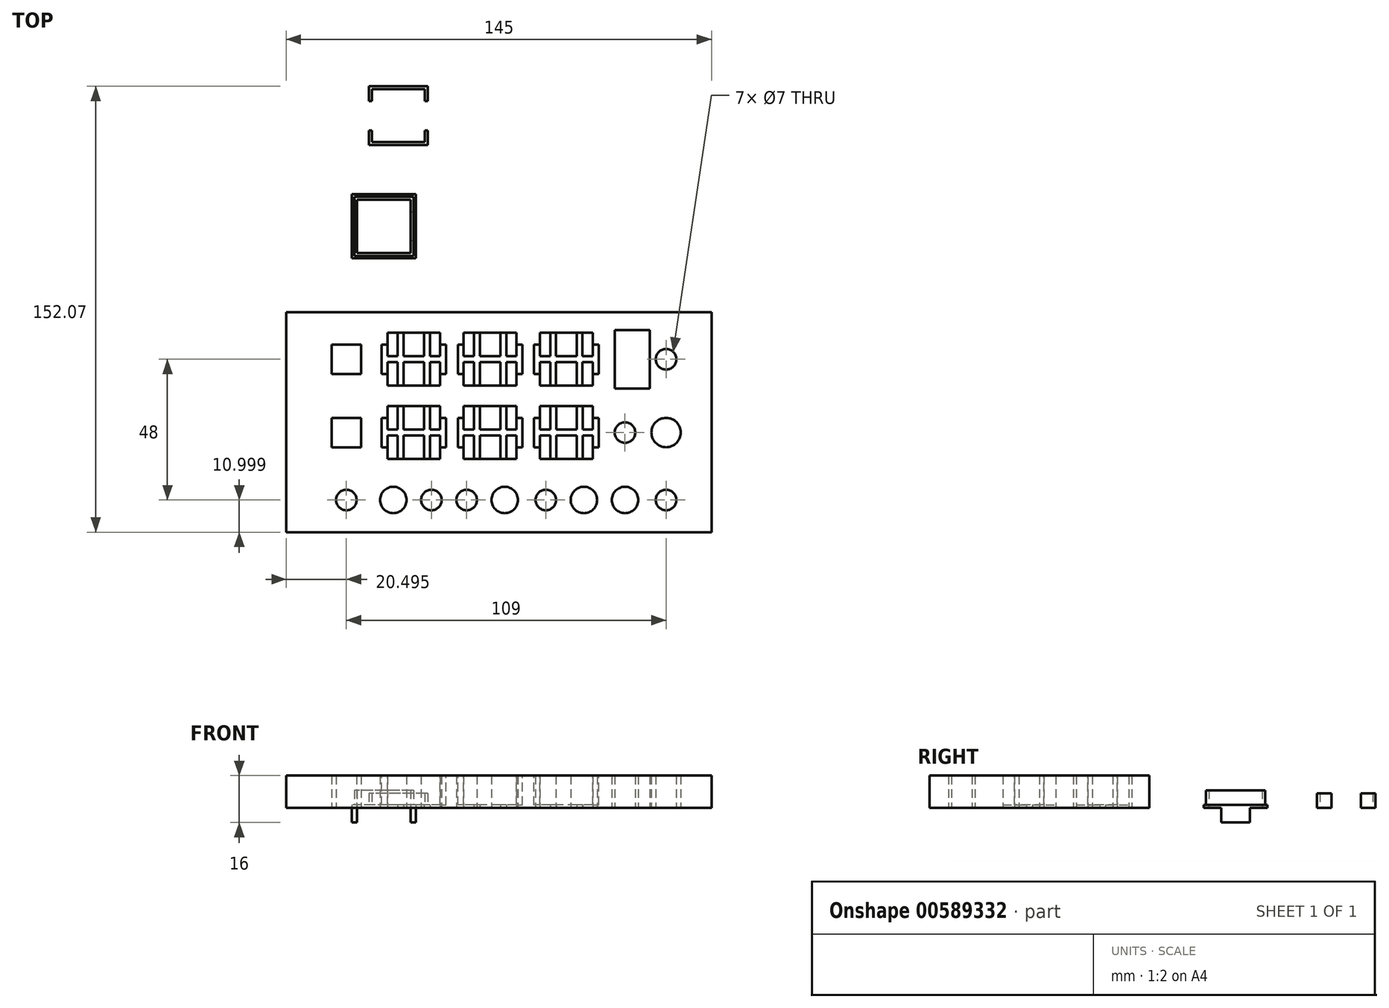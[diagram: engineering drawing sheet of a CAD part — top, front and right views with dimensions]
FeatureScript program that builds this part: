
annotation { "Feature Type Name" : "Feature", "Feature Type Description" : "" }
export const myFeature = defineFeature(function(context is Context, id is Id, definition is map)
    precondition{}
    {
        {
            var Q0;
            Q0=qCreatedBy(makeId("Top.planeOp"),FACE);
            var sketch = newSketch(context, id + "F0", { "sketchPlane" : qUnion([Q0])});
            skLineSegment(sketch, "E0.bottom", {"start": v(-10, -55.04) * mm, "end": v(-155, -55.04) * mm});
            skLineSegment(sketch, "E0.top", {"start": v(-10, 19.96) * mm, "end": v(-155, 19.96) * mm});
            skLineSegment(sketch, "E0.left", {"start": v(-10, -55.04) * mm, "end": v(-10, 19.96) * mm});
            skLineSegment(sketch, "E0.right", {"start": v(-155, -55.04) * mm, "end": v(-155, 19.96) * mm});
            skPoint(sketch, "E0.middle", {"position": v(-82.5, -17.54) * mm});
            skLineSegment(sketch, "E1.bottom", {"start": v(-101.5, -6.04) * mm, "end": v(-121.5, -6.04) * mm, "construction": true});
            skLineSegment(sketch, "E1.top", {"start": v(-101.5, 13.96) * mm, "end": v(-121.5, 13.96) * mm, "construction": true});
            skLineSegment(sketch, "E1.left", {"start": v(-101.5, -6.04) * mm, "end": v(-101.5, 13.96) * mm, "construction": true});
            skLineSegment(sketch, "E1.right", {"start": v(-121.5, -6.04) * mm, "end": v(-121.5, 13.96) * mm, "construction": true});
            skPoint(sketch, "E1.middle", {"position": v(-111.5, 3.96) * mm});
            skLineSegment(sketch, "E2.1.0.0", {"start": v(-95.5, -6.04) * mm, "end": v(-95.5, 13.96) * mm, "construction": true});
            skPoint(sketch, "E2.1.0.1", {"position": v(-85.5, 3.96) * mm});
            skLineSegment(sketch, "E2.1.0.2", {"start": v(-75.5, -6.04) * mm, "end": v(-95.5, -6.04) * mm, "construction": true});
            skLineSegment(sketch, "E2.1.0.3", {"start": v(-75.5, -6.04) * mm, "end": v(-75.5, 13.96) * mm, "construction": true});
            skLineSegment(sketch, "E2.1.0.4", {"start": v(-75.5, 13.96) * mm, "end": v(-95.5, 13.96) * mm, "construction": true});
            skLineSegment(sketch, "E2.2.0.0", {"start": v(-69.5, -6.04) * mm, "end": v(-69.5, 13.96) * mm, "construction": true});
            skPoint(sketch, "E2.2.0.1", {"position": v(-59.5, 3.96) * mm});
            skLineSegment(sketch, "E2.2.0.2", {"start": v(-49.5, -6.04) * mm, "end": v(-69.5, -6.04) * mm, "construction": true});
            skLineSegment(sketch, "E2.2.0.3", {"start": v(-49.5, -6.04) * mm, "end": v(-49.5, 13.96) * mm, "construction": true});
            skLineSegment(sketch, "E2.2.0.4", {"start": v(-49.5, 13.96) * mm, "end": v(-69.5, 13.96) * mm, "construction": true});
            skLineSegment(sketch, "E2.direction1", {"start": v(-121.5, -6.04) * mm, "end": v(-95.5, -6.04) * mm, "construction": true});
            skLineSegment(sketch, "E3.bottom", {"start": v(-101.5, -31.04) * mm, "end": v(-121.5, -31.04) * mm, "construction": true});
            skLineSegment(sketch, "E3.top", {"start": v(-101.5, -11.04) * mm, "end": v(-121.5, -11.04) * mm, "construction": true});
            skLineSegment(sketch, "E3.left", {"start": v(-101.5, -31.04) * mm, "end": v(-101.5, -11.04) * mm, "construction": true});
            skLineSegment(sketch, "E3.right", {"start": v(-121.5, -31.04) * mm, "end": v(-121.5, -11.04) * mm, "construction": true});
            skPoint(sketch, "E3.middle", {"position": v(-111.5, -21.04) * mm});
            skLineSegment(sketch, "E4.1.0.0", {"start": v(-75.5, -31.04) * mm, "end": v(-95.5, -31.04) * mm, "construction": true});
            skLineSegment(sketch, "E4.1.0.1", {"start": v(-75.5, -31.04) * mm, "end": v(-75.5, -11.04) * mm, "construction": true});
            skLineSegment(sketch, "E4.1.0.2", {"start": v(-95.5, -31.04) * mm, "end": v(-95.5, -11.04) * mm, "construction": true});
            skLineSegment(sketch, "E4.1.0.3", {"start": v(-75.5, -11.04) * mm, "end": v(-95.5, -11.04) * mm, "construction": true});
            skPoint(sketch, "E4.1.0.4", {"position": v(-85.5, -21.04) * mm});
            skLineSegment(sketch, "E4.2.0.0", {"start": v(-49.5, -31.04) * mm, "end": v(-69.5, -31.04) * mm, "construction": true});
            skLineSegment(sketch, "E4.2.0.1", {"start": v(-49.5, -31.04) * mm, "end": v(-49.5, -11.04) * mm, "construction": true});
            skLineSegment(sketch, "E4.2.0.2", {"start": v(-69.5, -31.04) * mm, "end": v(-69.5, -11.04) * mm, "construction": true});
            skLineSegment(sketch, "E4.2.0.3", {"start": v(-49.5, -11.04) * mm, "end": v(-69.5, -11.04) * mm, "construction": true});
            skPoint(sketch, "E4.2.0.4", {"position": v(-59.5, -21.04) * mm});
            skLineSegment(sketch, "E4.direction1", {"start": v(-121.5, -31.04) * mm, "end": v(-95.5, -31.04) * mm, "construction": true});
            skCircle(sketch, "E5", {"center": v(-134.5, -44.04) * mm, "radius": 3.5 * mm});
            skCircle(sketch, "E6", {"center": v(-105.5, -44.04) * mm, "radius": 3.5 * mm});
            skCircle(sketch, "E7", {"center": v(-93.5, -44.04) * mm, "radius": 3.5 * mm});
            skLineSegment(sketch, "E8.bottom", {"start": v(-155, 19.96) * mm, "end": v(-147, 19.96) * mm, "construction": true});
            skLineSegment(sketch, "E8.top", {"start": v(-155, -55.04) * mm, "end": v(-147, -55.04) * mm, "construction": true});
            skLineSegment(sketch, "E8.left", {"start": v(-155, 19.96) * mm, "end": v(-155, -55.04) * mm, "construction": true});
            skLineSegment(sketch, "E8.right", {"start": v(-147, 19.96) * mm, "end": v(-147, -55.04) * mm, "construction": true});
            skLineSegment(sketch, "E9.bottom", {"start": v(-10, -55.04) * mm, "end": v(-18, -55.04) * mm, "construction": true});
            skLineSegment(sketch, "E9.top", {"start": v(-10, 19.96) * mm, "end": v(-18, 19.96) * mm, "construction": true});
            skLineSegment(sketch, "E9.left", {"start": v(-10, -55.04) * mm, "end": v(-10, 19.96) * mm, "construction": true});
            skLineSegment(sketch, "E9.right", {"start": v(-18, -55.04) * mm, "end": v(-18, 19.96) * mm, "construction": true});
            skCircle(sketch, "E10", {"center": v(-118.5, -44.04) * mm, "radius": 4.5 * mm});
            skCircle(sketch, "E11", {"center": v(-80.5, -44.04) * mm, "radius": 4.5 * mm});
            skCircle(sketch, "E12", {"center": v(-66.5, -44.04) * mm, "radius": 3.5 * mm});
            skCircle(sketch, "E13", {"center": v(-53.5, -44.04) * mm, "radius": 4.5 * mm});
            skCircle(sketch, "E14", {"center": v(-39.5, -44.04) * mm, "radius": 4.5 * mm});
            skCircle(sketch, "E15", {"center": v(-25.5, -44.04) * mm, "radius": 3.5 * mm});
            skCircle(sketch, "E16", {"center": v(-39.5, -21.04) * mm, "radius": 3.5 * mm});
            skLineSegment(sketch, "E17.bottom", {"start": v(-31, -6.04) * mm, "end": v(-43, -6.04) * mm});
            skLineSegment(sketch, "E17.top", {"start": v(-31, 13.96) * mm, "end": v(-43, 13.96) * mm});
            skLineSegment(sketch, "E17.left", {"start": v(-31, -6.04) * mm, "end": v(-31, 13.96) * mm});
            skLineSegment(sketch, "E17.right", {"start": v(-43, -6.04) * mm, "end": v(-43, 13.96) * mm});
            skPoint(sketch, "E17.middle", {"position": v(-37, 3.96) * mm});
            skCircle(sketch, "E18", {"center": v(-25.5, 3.96) * mm, "radius": 3.5 * mm});
            skCircle(sketch, "E19", {"center": v(-25.5, -21.04) * mm, "radius": 5 * mm});
            skPoint(sketch, "E20.centerSnap0", {"position": v(-121.5, -21.04) * mm});
            skLineSegment(sketch, "E21.bottom", {"start": v(-102.5, -5.04) * mm, "end": v(-120.5, -5.04) * mm});
            skLineSegment(sketch, "E21.top", {"start": v(-102.5, 12.96) * mm, "end": v(-120.5, 12.96) * mm});
            skLineSegment(sketch, "E21.left", {"start": v(-102.5, -5.04) * mm, "end": v(-102.5, 12.96) * mm});
            skLineSegment(sketch, "E21.right", {"start": v(-120.5, -5.04) * mm, "end": v(-120.5, 12.96) * mm});
            skLineSegment(sketch, "E22.bottom", {"start": v(-102.5, -30.04) * mm, "end": v(-120.5, -30.04) * mm});
            skLineSegment(sketch, "E22.top", {"start": v(-102.5, -12.04) * mm, "end": v(-120.5, -12.04) * mm});
            skLineSegment(sketch, "E22.left", {"start": v(-102.5, -30.04) * mm, "end": v(-102.5, -12.04) * mm});
            skLineSegment(sketch, "E22.right", {"start": v(-120.5, -30.04) * mm, "end": v(-120.5, -12.04) * mm});
            skLineSegment(sketch, "E23.bottom", {"start": v(-102.5, 2.96) * mm, "end": v(-106, 2.96) * mm});
            skLineSegment(sketch, "E23.top", {"start": v(-102.5, 4.96) * mm, "end": v(-106, 4.96) * mm});
            skLineSegment(sketch, "E23.left", {"start": v(-102.5, 2.96) * mm, "end": v(-102.5, 4.96) * mm});
            skLineSegment(sketch, "E23.right", {"start": v(-120.5, 2.96) * mm, "end": v(-120.5, 4.96) * mm});
            skLineSegment(sketch, "E24.bottom", {"start": v(-115, -5.04) * mm, "end": v(-117, -5.04) * mm});
            skLineSegment(sketch, "E24.top", {"start": v(-115, 12.96) * mm, "end": v(-117, 12.96) * mm});
            skLineSegment(sketch, "E24.left", {"start": v(-115, -5.04) * mm, "end": v(-115, 2.96) * mm});
            skLineSegment(sketch, "E24.right", {"start": v(-117, -5.04) * mm, "end": v(-117, 2.96) * mm});
            skPoint(sketch, "E24.middle", {"position": v(-116, 3.96) * mm});
            skLineSegment(sketch, "E25.bottom", {"start": v(-106, -5.04) * mm, "end": v(-108, -5.04) * mm});
            skLineSegment(sketch, "E25.top", {"start": v(-106, 12.96) * mm, "end": v(-108, 12.96) * mm});
            skLineSegment(sketch, "E25.left", {"start": v(-106, -5.04) * mm, "end": v(-106, 2.96) * mm});
            skLineSegment(sketch, "E25.right", {"start": v(-108, -5.04) * mm, "end": v(-108, 2.96) * mm});
            skPoint(sketch, "E25.middle", {"position": v(-107, 3.96) * mm});
            skLineSegment(sketch, "E26.trimOffspring", {"start": v(-117, 4.96) * mm, "end": v(-117, 12.96) * mm});
            skLineSegment(sketch, "E27.trimOffspring", {"start": v(-117, 4.96) * mm, "end": v(-120.5, 4.96) * mm});
            skLineSegment(sketch, "E28.trimOffspring", {"start": v(-115, 4.96) * mm, "end": v(-115, 12.96) * mm});
            skLineSegment(sketch, "E29.trimOffspring", {"start": v(-117, 2.96) * mm, "end": v(-120.5, 2.96) * mm});
            skLineSegment(sketch, "E30.trimOffspring", {"start": v(-108, 4.96) * mm, "end": v(-108, 12.96) * mm});
            skLineSegment(sketch, "E31.trimOffspring", {"start": v(-108, 4.96) * mm, "end": v(-115, 4.96) * mm});
            skLineSegment(sketch, "E32.trimOffspring", {"start": v(-106, 4.96) * mm, "end": v(-106, 12.96) * mm});
            skLineSegment(sketch, "E33.trimOffspring", {"start": v(-108, 2.96) * mm, "end": v(-115, 2.96) * mm});
            skLineSegment(sketch, "E34.bottom", {"start": v(-131, -50.54) * mm, "end": v(-138, -50.54) * mm, "construction": true});
            skLineSegment(sketch, "E34.top", {"start": v(-131, -37.54) * mm, "end": v(-138, -37.54) * mm, "construction": true});
            skLineSegment(sketch, "E34.left", {"start": v(-131, -50.54) * mm, "end": v(-131, -37.54) * mm, "construction": true});
            skLineSegment(sketch, "E34.right", {"start": v(-138, -50.54) * mm, "end": v(-138, -37.54) * mm, "construction": true});
            skLineSegment(sketch, "E35.bottom", {"start": v(-102.5, -22.04) * mm, "end": v(-105.98, -22.04) * mm});
            skLineSegment(sketch, "E35.top", {"start": v(-102.5, -20.04) * mm, "end": v(-105.98, -20.04) * mm});
            skLineSegment(sketch, "E35.left", {"start": v(-102.5, -22.04) * mm, "end": v(-102.5, -20.04) * mm});
            skLineSegment(sketch, "E35.right", {"start": v(-120.5, -22.04) * mm, "end": v(-120.5, -20.04) * mm});
            skLineSegment(sketch, "E36.bottom", {"start": v(-114.98, -30.04) * mm, "end": v(-116.98, -30.04) * mm});
            skLineSegment(sketch, "E36.top", {"start": v(-114.98, -12.04) * mm, "end": v(-116.98, -12.04) * mm});
            skLineSegment(sketch, "E36.left", {"start": v(-114.98, -30.04) * mm, "end": v(-114.98, -22.04) * mm});
            skLineSegment(sketch, "E36.right", {"start": v(-116.98, -30.04) * mm, "end": v(-116.98, -22.04) * mm});
            skPoint(sketch, "E36.middle", {"position": v(-115.98, -21.04) * mm});
            skLineSegment(sketch, "E37.bottom", {"start": v(-105.98, -30.04) * mm, "end": v(-107.98, -30.04) * mm});
            skLineSegment(sketch, "E37.top", {"start": v(-105.98, -12.04) * mm, "end": v(-107.98, -12.04) * mm});
            skLineSegment(sketch, "E37.left", {"start": v(-105.98, -30.04) * mm, "end": v(-105.98, -22.04) * mm});
            skLineSegment(sketch, "E37.right", {"start": v(-107.98, -30.04) * mm, "end": v(-107.98, -22.04) * mm});
            skPoint(sketch, "E37.middle", {"position": v(-106.98, -21.04) * mm});
            skLineSegment(sketch, "E38.trimOffspring", {"start": v(-116.98, -20.04) * mm, "end": v(-116.98, -12.04) * mm});
            skLineSegment(sketch, "E39.trimOffspring", {"start": v(-116.98, -20.04) * mm, "end": v(-120.5, -20.04) * mm});
            skLineSegment(sketch, "E40.trimOffspring", {"start": v(-114.98, -20.04) * mm, "end": v(-114.98, -12.04) * mm});
            skLineSegment(sketch, "E41.trimOffspring", {"start": v(-116.98, -22.04) * mm, "end": v(-120.5, -22.04) * mm});
            skLineSegment(sketch, "E42.trimOffspring", {"start": v(-107.98, -20.04) * mm, "end": v(-107.98, -12.04) * mm});
            skLineSegment(sketch, "E43.trimOffspring", {"start": v(-107.98, -20.04) * mm, "end": v(-114.98, -20.04) * mm});
            skLineSegment(sketch, "E44.trimOffspring", {"start": v(-105.98, -20.04) * mm, "end": v(-105.98, -12.04) * mm});
            skLineSegment(sketch, "E45.trimOffspring", {"start": v(-107.98, -22.04) * mm, "end": v(-114.98, -22.04) * mm});
            skLineSegment(sketch, "E46.bottom", {"start": v(-129.5, -1.04) * mm, "end": v(-139.5, -1.04) * mm});
            skLineSegment(sketch, "E46.top", {"start": v(-129.5, 8.96) * mm, "end": v(-139.5, 8.96) * mm});
            skLineSegment(sketch, "E46.left", {"start": v(-129.5, -1.04) * mm, "end": v(-129.5, 8.96) * mm});
            skLineSegment(sketch, "E46.right", {"start": v(-139.5, -1.04) * mm, "end": v(-139.5, 8.96) * mm});
            skPoint(sketch, "E46.middle", {"position": v(-134.5, 3.96) * mm});
            skLineSegment(sketch, "E47.bottom", {"start": v(-129.5, -26.04) * mm, "end": v(-139.5, -26.04) * mm});
            skLineSegment(sketch, "E47.top", {"start": v(-129.5, -16.04) * mm, "end": v(-139.5, -16.04) * mm});
            skLineSegment(sketch, "E47.left", {"start": v(-129.5, -26.04) * mm, "end": v(-129.5, -16.04) * mm});
            skLineSegment(sketch, "E47.right", {"start": v(-139.5, -26.04) * mm, "end": v(-139.5, -16.04) * mm});
            skPoint(sketch, "E47.middle", {"position": v(-134.5, -21.04) * mm});
            skLineSegment(sketch, "E48.1.0.0", {"start": v(-91, 4.96) * mm, "end": v(-91, 12.96) * mm});
            skLineSegment(sketch, "E48.1.0.2", {"start": v(-76.5, -5.04) * mm, "end": v(-76.5, 12.96) * mm});
            skLineSegment(sketch, "E48.1.0.3", {"start": v(-80, -5.04) * mm, "end": v(-80, 2.96) * mm});
            skPoint(sketch, "E48.1.0.4", {"position": v(-90, 3.96) * mm});
            skLineSegment(sketch, "E48.1.0.5", {"start": v(-82, 4.96) * mm, "end": v(-82, 12.96) * mm});
            skLineSegment(sketch, "E48.1.0.6", {"start": v(-80, 4.96) * mm, "end": v(-80, 12.96) * mm});
            skLineSegment(sketch, "E48.1.0.7", {"start": v(-82, 4.96) * mm, "end": v(-89, 4.96) * mm});
            skLineSegment(sketch, "E48.1.0.8", {"start": v(-76.5, 4.96) * mm, "end": v(-80, 4.96) * mm});
            skLineSegment(sketch, "E48.1.0.9", {"start": v(-76.5, 2.96) * mm, "end": v(-80, 2.96) * mm});
            skLineSegment(sketch, "E48.1.0.10", {"start": v(-80, 12.96) * mm, "end": v(-82, 12.96) * mm});
            skPoint(sketch, "E48.1.0.11", {"position": v(-81, 3.96) * mm});
            skLineSegment(sketch, "E48.1.0.12", {"start": v(-91, 4.96) * mm, "end": v(-94.5, 4.96) * mm});
            skLineSegment(sketch, "E48.1.0.13", {"start": v(-91, 2.96) * mm, "end": v(-94.5, 2.96) * mm});
            skLineSegment(sketch, "E48.1.0.14", {"start": v(-89, 4.96) * mm, "end": v(-89, 12.96) * mm});
            skLineSegment(sketch, "E48.1.0.15", {"start": v(-76.5, 12.96) * mm, "end": v(-94.5, 12.96) * mm});
            skLineSegment(sketch, "E48.1.0.16", {"start": v(-91, -5.04) * mm, "end": v(-91, 2.96) * mm});
            skLineSegment(sketch, "E48.1.0.17", {"start": v(-76.5, -5.04) * mm, "end": v(-94.5, -5.04) * mm});
            skLineSegment(sketch, "E48.1.0.18", {"start": v(-89, -5.04) * mm, "end": v(-89, 2.96) * mm});
            skLineSegment(sketch, "E48.1.0.19", {"start": v(-82, -5.04) * mm, "end": v(-82, 2.96) * mm});
            skLineSegment(sketch, "E48.1.0.20", {"start": v(-94.5, -5.04) * mm, "end": v(-94.5, 12.96) * mm});
            skLineSegment(sketch, "E48.1.0.21", {"start": v(-82, 2.96) * mm, "end": v(-89, 2.96) * mm});
            skLineSegment(sketch, "E48.1.0.22", {"start": v(-80, -5.04) * mm, "end": v(-82, -5.04) * mm});
            skLineSegment(sketch, "E48.1.0.23", {"start": v(-76.5, 2.96) * mm, "end": v(-76.5, 4.96) * mm});
            skLineSegment(sketch, "E48.1.0.24", {"start": v(-89, -5.04) * mm, "end": v(-91, -5.04) * mm});
            skLineSegment(sketch, "E48.1.0.25", {"start": v(-94.5, 2.96) * mm, "end": v(-94.5, 4.96) * mm});
            skLineSegment(sketch, "E48.1.0.27", {"start": v(-89, 12.96) * mm, "end": v(-91, 12.96) * mm});
            skLineSegment(sketch, "E48.2.0.0", {"start": v(-65, 4.96) * mm, "end": v(-65, 12.96) * mm});
            skLineSegment(sketch, "E48.2.0.2", {"start": v(-50.5, -5.04) * mm, "end": v(-50.5, 12.96) * mm});
            skLineSegment(sketch, "E48.2.0.3", {"start": v(-54, -5.04) * mm, "end": v(-54, 2.96) * mm});
            skPoint(sketch, "E48.2.0.4", {"position": v(-64, 3.96) * mm});
            skLineSegment(sketch, "E48.2.0.5", {"start": v(-56, 4.96) * mm, "end": v(-56, 12.96) * mm});
            skLineSegment(sketch, "E48.2.0.6", {"start": v(-54, 4.96) * mm, "end": v(-54, 12.96) * mm});
            skLineSegment(sketch, "E48.2.0.7", {"start": v(-56, 4.96) * mm, "end": v(-63, 4.96) * mm});
            skLineSegment(sketch, "E48.2.0.8", {"start": v(-50.5, 4.96) * mm, "end": v(-54, 4.96) * mm});
            skLineSegment(sketch, "E48.2.0.9", {"start": v(-50.5, 2.96) * mm, "end": v(-54, 2.96) * mm});
            skLineSegment(sketch, "E48.2.0.10", {"start": v(-54, 12.96) * mm, "end": v(-56, 12.96) * mm});
            skPoint(sketch, "E48.2.0.11", {"position": v(-55, 3.96) * mm});
            skLineSegment(sketch, "E48.2.0.12", {"start": v(-65, 4.96) * mm, "end": v(-68.5, 4.96) * mm});
            skLineSegment(sketch, "E48.2.0.13", {"start": v(-65, 2.96) * mm, "end": v(-68.5, 2.96) * mm});
            skLineSegment(sketch, "E48.2.0.14", {"start": v(-63, 4.96) * mm, "end": v(-63, 12.96) * mm});
            skLineSegment(sketch, "E48.2.0.15", {"start": v(-50.5, 12.96) * mm, "end": v(-68.5, 12.96) * mm});
            skLineSegment(sketch, "E48.2.0.16", {"start": v(-65, -5.04) * mm, "end": v(-65, 2.96) * mm});
            skLineSegment(sketch, "E48.2.0.17", {"start": v(-50.5, -5.04) * mm, "end": v(-68.5, -5.04) * mm});
            skLineSegment(sketch, "E48.2.0.18", {"start": v(-63, -5.04) * mm, "end": v(-63, 2.96) * mm});
            skLineSegment(sketch, "E48.2.0.19", {"start": v(-56, -5.04) * mm, "end": v(-56, 2.96) * mm});
            skLineSegment(sketch, "E48.2.0.20", {"start": v(-68.5, -5.04) * mm, "end": v(-68.5, 12.96) * mm});
            skLineSegment(sketch, "E48.2.0.21", {"start": v(-56, 2.96) * mm, "end": v(-63, 2.96) * mm});
            skLineSegment(sketch, "E48.2.0.22", {"start": v(-54, -5.04) * mm, "end": v(-56, -5.04) * mm});
            skLineSegment(sketch, "E48.2.0.23", {"start": v(-50.5, 2.96) * mm, "end": v(-50.5, 4.96) * mm});
            skLineSegment(sketch, "E48.2.0.24", {"start": v(-63, -5.04) * mm, "end": v(-65, -5.04) * mm});
            skLineSegment(sketch, "E48.2.0.25", {"start": v(-68.5, 2.96) * mm, "end": v(-68.5, 4.96) * mm});
            skLineSegment(sketch, "E48.2.0.27", {"start": v(-63, 12.96) * mm, "end": v(-65, 12.96) * mm});
            skLineSegment(sketch, "E48.direction1", {"start": v(-120.5, -5.04) * mm, "end": v(-94.5, -5.04) * mm, "construction": true});
            skLineSegment(sketch, "E49.1.0.0", {"start": v(-76.5, -20.04) * mm, "end": v(-79.98, -20.04) * mm});
            skLineSegment(sketch, "E49.1.0.1", {"start": v(-88.98, -20.04) * mm, "end": v(-88.98, -12.04) * mm});
            skLineSegment(sketch, "E49.1.0.2", {"start": v(-81.98, -30.04) * mm, "end": v(-81.98, -22.04) * mm});
            skLineSegment(sketch, "E49.1.0.3", {"start": v(-94.5, -30.04) * mm, "end": v(-94.5, -12.04) * mm});
            skLineSegment(sketch, "E49.1.0.4", {"start": v(-90.98, -30.04) * mm, "end": v(-90.98, -22.04) * mm});
            skLineSegment(sketch, "E49.1.0.5", {"start": v(-76.5, -30.04) * mm, "end": v(-76.5, -12.04) * mm});
            skLineSegment(sketch, "E49.1.0.6", {"start": v(-81.98, -22.04) * mm, "end": v(-88.98, -22.04) * mm});
            skLineSegment(sketch, "E49.1.0.7", {"start": v(-88.98, -30.04) * mm, "end": v(-88.98, -22.04) * mm});
            skLineSegment(sketch, "E49.1.0.9", {"start": v(-79.98, -20.04) * mm, "end": v(-79.98, -12.04) * mm});
            skLineSegment(sketch, "E49.1.0.10", {"start": v(-76.5, -22.04) * mm, "end": v(-79.98, -22.04) * mm});
            skPoint(sketch, "E49.1.0.11", {"position": v(-80.98, -21.04) * mm});
            skLineSegment(sketch, "E49.1.0.12", {"start": v(-90.98, -22.04) * mm, "end": v(-94.5, -22.04) * mm});
            skLineSegment(sketch, "E49.1.0.14", {"start": v(-81.98, -20.04) * mm, "end": v(-88.98, -20.04) * mm});
            skPoint(sketch, "E49.1.0.15", {"position": v(-89.98, -21.04) * mm});
            skLineSegment(sketch, "E49.1.0.16", {"start": v(-79.98, -30.04) * mm, "end": v(-79.98, -22.04) * mm});
            skLineSegment(sketch, "E49.1.0.17", {"start": v(-76.5, -30.04) * mm, "end": v(-94.5, -30.04) * mm});
            skLineSegment(sketch, "E49.1.0.18", {"start": v(-90.98, -20.04) * mm, "end": v(-90.98, -12.04) * mm});
            skLineSegment(sketch, "E49.1.0.19", {"start": v(-81.98, -20.04) * mm, "end": v(-81.98, -12.04) * mm});
            skLineSegment(sketch, "E49.1.0.20", {"start": v(-90.98, -20.04) * mm, "end": v(-94.5, -20.04) * mm});
            skLineSegment(sketch, "E49.1.0.21", {"start": v(-76.5, -12.04) * mm, "end": v(-94.5, -12.04) * mm});
            skLineSegment(sketch, "E49.1.0.22", {"start": v(-88.98, -12.04) * mm, "end": v(-90.98, -12.04) * mm});
            skLineSegment(sketch, "E49.1.0.23", {"start": v(-76.5, -22.04) * mm, "end": v(-76.5, -20.04) * mm});
            skLineSegment(sketch, "E49.1.0.24", {"start": v(-94.5, -22.04) * mm, "end": v(-94.5, -20.04) * mm});
            skLineSegment(sketch, "E49.1.0.26", {"start": v(-94.5, -30.04) * mm, "end": v(-94.5, -12.04) * mm});
            skLineSegment(sketch, "E49.1.0.27", {"start": v(-79.98, -12.04) * mm, "end": v(-81.98, -12.04) * mm});
            skLineSegment(sketch, "E49.1.0.28", {"start": v(-76.5, -30.04) * mm, "end": v(-94.5, -30.04) * mm});
            skLineSegment(sketch, "E49.1.0.29", {"start": v(-76.5, -12.04) * mm, "end": v(-94.5, -12.04) * mm});
            skLineSegment(sketch, "E49.1.0.30", {"start": v(-76.5, -30.04) * mm, "end": v(-76.5, -12.04) * mm});
            skLineSegment(sketch, "E49.1.0.31", {"start": v(-88.98, -30.04) * mm, "end": v(-90.98, -30.04) * mm});
            skLineSegment(sketch, "E49.1.0.32", {"start": v(-79.98, -30.04) * mm, "end": v(-81.98, -30.04) * mm});
            skLineSegment(sketch, "E49.2.0.0", {"start": v(-50.5, -20.04) * mm, "end": v(-53.98, -20.04) * mm});
            skLineSegment(sketch, "E49.2.0.1", {"start": v(-62.98, -20.04) * mm, "end": v(-62.98, -12.04) * mm});
            skLineSegment(sketch, "E49.2.0.2", {"start": v(-55.98, -30.04) * mm, "end": v(-55.98, -22.04) * mm});
            skLineSegment(sketch, "E49.2.0.3", {"start": v(-68.5, -30.04) * mm, "end": v(-68.5, -12.04) * mm});
            skLineSegment(sketch, "E49.2.0.4", {"start": v(-64.98, -30.04) * mm, "end": v(-64.98, -22.04) * mm});
            skLineSegment(sketch, "E49.2.0.5", {"start": v(-50.5, -30.04) * mm, "end": v(-50.5, -12.04) * mm});
            skLineSegment(sketch, "E49.2.0.6", {"start": v(-55.98, -22.04) * mm, "end": v(-62.98, -22.04) * mm});
            skLineSegment(sketch, "E49.2.0.7", {"start": v(-62.98, -30.04) * mm, "end": v(-62.98, -22.04) * mm});
            skLineSegment(sketch, "E49.2.0.9", {"start": v(-53.98, -20.04) * mm, "end": v(-53.98, -12.04) * mm});
            skLineSegment(sketch, "E49.2.0.10", {"start": v(-50.5, -22.04) * mm, "end": v(-53.98, -22.04) * mm});
            skPoint(sketch, "E49.2.0.11", {"position": v(-54.98, -21.04) * mm});
            skLineSegment(sketch, "E49.2.0.12", {"start": v(-64.98, -22.04) * mm, "end": v(-68.5, -22.04) * mm});
            skLineSegment(sketch, "E49.2.0.14", {"start": v(-55.98, -20.04) * mm, "end": v(-62.98, -20.04) * mm});
            skPoint(sketch, "E49.2.0.15", {"position": v(-63.98, -21.04) * mm});
            skLineSegment(sketch, "E49.2.0.16", {"start": v(-53.98, -30.04) * mm, "end": v(-53.98, -22.04) * mm});
            skLineSegment(sketch, "E49.2.0.17", {"start": v(-50.5, -30.04) * mm, "end": v(-68.5, -30.04) * mm});
            skLineSegment(sketch, "E49.2.0.18", {"start": v(-64.98, -20.04) * mm, "end": v(-64.98, -12.04) * mm});
            skLineSegment(sketch, "E49.2.0.19", {"start": v(-55.98, -20.04) * mm, "end": v(-55.98, -12.04) * mm});
            skLineSegment(sketch, "E49.2.0.20", {"start": v(-64.98, -20.04) * mm, "end": v(-68.5, -20.04) * mm});
            skLineSegment(sketch, "E49.2.0.21", {"start": v(-50.5, -12.04) * mm, "end": v(-68.5, -12.04) * mm});
            skLineSegment(sketch, "E49.2.0.22", {"start": v(-62.98, -12.04) * mm, "end": v(-64.98, -12.04) * mm});
            skLineSegment(sketch, "E49.2.0.23", {"start": v(-50.5, -22.04) * mm, "end": v(-50.5, -20.04) * mm});
            skLineSegment(sketch, "E49.2.0.24", {"start": v(-68.5, -22.04) * mm, "end": v(-68.5, -20.04) * mm});
            skLineSegment(sketch, "E49.2.0.26", {"start": v(-68.5, -30.04) * mm, "end": v(-68.5, -12.04) * mm});
            skLineSegment(sketch, "E49.2.0.27", {"start": v(-53.98, -12.04) * mm, "end": v(-55.98, -12.04) * mm});
            skLineSegment(sketch, "E49.2.0.28", {"start": v(-50.5, -30.04) * mm, "end": v(-68.5, -30.04) * mm});
            skLineSegment(sketch, "E49.2.0.29", {"start": v(-50.5, -12.04) * mm, "end": v(-68.5, -12.04) * mm});
            skLineSegment(sketch, "E49.2.0.30", {"start": v(-50.5, -30.04) * mm, "end": v(-50.5, -12.04) * mm});
            skLineSegment(sketch, "E49.2.0.31", {"start": v(-62.98, -30.04) * mm, "end": v(-64.98, -30.04) * mm});
            skLineSegment(sketch, "E49.2.0.32", {"start": v(-53.98, -30.04) * mm, "end": v(-55.98, -30.04) * mm});
            skLineSegment(sketch, "E49.direction1", {"start": v(-120.5, -30.04) * mm, "end": v(-94.5, -30.04) * mm, "construction": true});
            skLineSegment(sketch, "E50.bottom", {"start": v(-133, -1.04) * mm, "end": v(-136, -1.04) * mm});
            skLineSegment(sketch, "E50.top", {"start": v(-133, 8.96) * mm, "end": v(-136, 8.96) * mm});
            skLineSegment(sketch, "E50.left", {"start": v(-133, -1.04) * mm, "end": v(-133, 8.96) * mm});
            skLineSegment(sketch, "E50.right", {"start": v(-136, -1.04) * mm, "end": v(-136, 8.96) * mm});
            skLineSegment(sketch, "E51.bottom", {"start": v(-133, -26.04) * mm, "end": v(-136, -26.04) * mm});
            skLineSegment(sketch, "E51.top", {"start": v(-133, -16.04) * mm, "end": v(-136, -16.04) * mm});
            skLineSegment(sketch, "E51.left", {"start": v(-133, -26.04) * mm, "end": v(-133, -16.04) * mm});
            skLineSegment(sketch, "E51.right", {"start": v(-136, -26.04) * mm, "end": v(-136, -16.04) * mm});
            skSolve(sketch);
        }
        {
            var Q0;
            Q0=makeQuery(id+"F0.imprint","IMPRINT",FACE,{"disambiguationData":[TD([[makeQuery(id+"F0.imprint","IMPRINT",EDGE,{"derivedFrom":sQuery(id+"F0.wireOp",EDGE,"E0.bottom")}),-1.0]])]});
            var Q1;
            Q1=makeQuery(id+"F0.imprint","IMPRINT",FACE,{"disambiguationData":[TD([[makeQuery(id+"F0.imprint","IMPRINT",EDGE,{"derivedFrom":sQuery(id+"F0.wireOp",EDGE,"E23.bottom")}),-1.0]])]});
            var Q2;
            Q2=makeQuery(id+"F0.imprint","IMPRINT",FACE,{"disambiguationData":[TD([[makeQuery(id+"F0.imprint","IMPRINT",EDGE,{"derivedFrom":sQuery(id+"F0.wireOp",EDGE,"E35.bottom")}),-1.0]])]});
            var Q3;
            Q3=makeQuery(id+"F0.imprint","IMPRINT",FACE,{"disambiguationData":[TD([[makeQuery(id+"F0.imprint","IMPRINT",EDGE,{"derivedFrom":sQuery(id+"F0.wireOp",EDGE,"E48.1.0.0")}),-1.0]])]});
            var Q4;
            Q4=makeQuery(id+"F0.imprint","IMPRINT",FACE,{"disambiguationData":[TD([[makeQuery(id+"F0.imprint","IMPRINT",EDGE,{"derivedFrom":sQuery(id+"F0.wireOp",EDGE,"E48.2.0.0")}),-1.0]])]});
            var Q5;
            {var subQ3=sQuery(id+"F0.wireOp",EDGE,"E49.2.0.0");Q5=makeQuery(id+"F0.imprint","IMPRINT",FACE,{"disambiguationData":[TD([[makeQuery(id+"F0.imprint","IMPRINT",EDGE,{"derivedFrom":subQ3}),1.0]])]});}
            var Q6;
            {var subQ3=sQuery(id+"F0.wireOp",EDGE,"E49.1.0.0");Q6=makeQuery(id+"F0.imprint","IMPRINT",FACE,{"disambiguationData":[TD([[makeQuery(id+"F0.imprint","IMPRINT",EDGE,{"derivedFrom":subQ3}),1.0]])]});}
            var Q7;
            Q7=makeQuery(id+"F0.imprint","IMPRINT",FACE,{"disambiguationData":[TD([[makeQuery(id+"F0.imprint","IMPRINT",EDGE,{"derivedFrom":sQuery(id+"F0.wireOp",EDGE,"E50.bottom")}),-1.0]])]});
            var Q8;
            Q8=makeQuery(id+"F0.imprint","IMPRINT",FACE,{"disambiguationData":[TD([[makeQuery(id+"F0.imprint","IMPRINT",EDGE,{"derivedFrom":sQuery(id+"F0.wireOp",EDGE,"E51.bottom")}),-1.0]])]});
            extrude(context, id + "F1", {"entities" : qUnion([Q0, Q1, Q2, Q3, Q4, Q5, Q6, Q7, Q8]), "depth" : 1 * mm});
        }
        {
            var Q0;
            Q0=makeQuery(id+"F1.opExtrude","CAP_FACE",FACE,{"disambiguationData":[OSD([sQuery(id+"F0.wireOp",EDGE,"E0.bottom"),sQuery(id+"F0.wireOp",EDGE,"E0.top"),sQuery(id+"F0.wireOp",EDGE,"E0.left"),sQuery(id+"F0.wireOp",EDGE,"E0.right"),sQuery(id+"F0.wireOp",EDGE,"E5"),sQuery(id+"F0.wireOp",EDGE,"E6"),sQuery(id+"F0.wireOp",EDGE,"E7"),sQuery(id+"F0.wireOp",EDGE,"E10"),sQuery(id+"F0.wireOp",EDGE,"E11"),sQuery(id+"F0.wireOp",EDGE,"E12"),sQuery(id+"F0.wireOp",EDGE,"E13"),sQuery(id+"F0.wireOp",EDGE,"E14"),sQuery(id+"F0.wireOp",EDGE,"E15"),sQuery(id+"F0.wireOp",EDGE,"E16"),sQuery(id+"F0.wireOp",EDGE,"E17.bottom"),sQuery(id+"F0.wireOp",EDGE,"E17.top"),sQuery(id+"F0.wireOp",EDGE,"E17.left"),sQuery(id+"F0.wireOp",EDGE,"E17.right"),sQuery(id+"F0.wireOp",EDGE,"E18"),sQuery(id+"F0.wireOp",EDGE,"E19"),sQuery(id+"F0.wireOp",EDGE,"E21.bottom"),sQuery(id+"F0.wireOp",EDGE,"E21.top"),sQuery(id+"F0.wireOp",EDGE,"E21.left"),sQuery(id+"F0.wireOp",EDGE,"E21.right"),sQuery(id+"F0.wireOp",EDGE,"E23.bottom"),sQuery(id+"F0.wireOp",EDGE,"E23.top"),sQuery(id+"F0.wireOp",EDGE,"E24.left"),sQuery(id+"F0.wireOp",EDGE,"E24.right"),sQuery(id+"F0.wireOp",EDGE,"E25.left"),sQuery(id+"F0.wireOp",EDGE,"E25.right"),sQuery(id+"F0.wireOp",EDGE,"E26.trimOffspring"),sQuery(id+"F0.wireOp",EDGE,"E27.trimOffspring"),sQuery(id+"F0.wireOp",EDGE,"E28.trimOffspring"),sQuery(id+"F0.wireOp",EDGE,"E29.trimOffspring"),sQuery(id+"F0.wireOp",EDGE,"E30.trimOffspring"),sQuery(id+"F0.wireOp",EDGE,"E31.trimOffspring"),sQuery(id+"F0.wireOp",EDGE,"E32.trimOffspring"),sQuery(id+"F0.wireOp",EDGE,"E33.trimOffspring"),sQuery(id+"F0.wireOp",EDGE,"E22.bottom"),sQuery(id+"F0.wireOp",EDGE,"E22.top"),sQuery(id+"F0.wireOp",EDGE,"E22.left"),sQuery(id+"F0.wireOp",EDGE,"E22.right"),sQuery(id+"F0.wireOp",EDGE,"E35.bottom"),sQuery(id+"F0.wireOp",EDGE,"E35.top"),sQuery(id+"F0.wireOp",EDGE,"E36.left"),sQuery(id+"F0.wireOp",EDGE,"E36.right"),sQuery(id+"F0.wireOp",EDGE,"E37.left"),sQuery(id+"F0.wireOp",EDGE,"E37.right"),sQuery(id+"F0.wireOp",EDGE,"E38.trimOffspring"),sQuery(id+"F0.wireOp",EDGE,"E39.trimOffspring"),sQuery(id+"F0.wireOp",EDGE,"E40.trimOffspring"),sQuery(id+"F0.wireOp",EDGE,"E41.trimOffspring"),sQuery(id+"F0.wireOp",EDGE,"E42.trimOffspring"),sQuery(id+"F0.wireOp",EDGE,"E43.trimOffspring"),sQuery(id+"F0.wireOp",EDGE,"E44.trimOffspring"),sQuery(id+"F0.wireOp",EDGE,"E45.trimOffspring"),sQuery(id+"F0.wireOp",EDGE,"E46.bottom"),sQuery(id+"F0.wireOp",EDGE,"E46.top"),sQuery(id+"F0.wireOp",EDGE,"E46.left"),sQuery(id+"F0.wireOp",EDGE,"E46.right"),sQuery(id+"F0.wireOp",EDGE,"E47.bottom"),sQuery(id+"F0.wireOp",EDGE,"E47.top"),sQuery(id+"F0.wireOp",EDGE,"E47.left"),sQuery(id+"F0.wireOp",EDGE,"E47.right"),sQuery(id+"F0.wireOp",EDGE,"E48.1.0.0"),sQuery(id+"F0.wireOp",EDGE,"E48.1.0.2"),sQuery(id+"F0.wireOp",EDGE,"E48.1.0.3"),sQuery(id+"F0.wireOp",EDGE,"E48.1.0.5"),sQuery(id+"F0.wireOp",EDGE,"E48.1.0.6"),sQuery(id+"F0.wireOp",EDGE,"E48.1.0.7"),sQuery(id+"F0.wireOp",EDGE,"E48.1.0.8"),sQuery(id+"F0.wireOp",EDGE,"E48.1.0.9"),sQuery(id+"F0.wireOp",EDGE,"E48.1.0.12"),sQuery(id+"F0.wireOp",EDGE,"E48.1.0.13"),sQuery(id+"F0.wireOp",EDGE,"E48.1.0.14"),sQuery(id+"F0.wireOp",EDGE,"E48.1.0.15"),sQuery(id+"F0.wireOp",EDGE,"E48.1.0.16"),sQuery(id+"F0.wireOp",EDGE,"E48.1.0.17"),sQuery(id+"F0.wireOp",EDGE,"E48.1.0.18"),sQuery(id+"F0.wireOp",EDGE,"E48.1.0.19"),sQuery(id+"F0.wireOp",EDGE,"E48.1.0.20"),sQuery(id+"F0.wireOp",EDGE,"E48.1.0.21"),sQuery(id+"F0.wireOp",EDGE,"E48.2.0.0"),sQuery(id+"F0.wireOp",EDGE,"E48.2.0.2"),sQuery(id+"F0.wireOp",EDGE,"E48.2.0.3"),sQuery(id+"F0.wireOp",EDGE,"E48.2.0.5"),sQuery(id+"F0.wireOp",EDGE,"E48.2.0.6"),sQuery(id+"F0.wireOp",EDGE,"E48.2.0.7"),sQuery(id+"F0.wireOp",EDGE,"E48.2.0.8"),sQuery(id+"F0.wireOp",EDGE,"E48.2.0.9"),sQuery(id+"F0.wireOp",EDGE,"E48.2.0.12"),sQuery(id+"F0.wireOp",EDGE,"E48.2.0.13"),sQuery(id+"F0.wireOp",EDGE,"E48.2.0.14"),sQuery(id+"F0.wireOp",EDGE,"E48.2.0.15"),sQuery(id+"F0.wireOp",EDGE,"E48.2.0.16"),sQuery(id+"F0.wireOp",EDGE,"E48.2.0.17"),sQuery(id+"F0.wireOp",EDGE,"E48.2.0.18"),sQuery(id+"F0.wireOp",EDGE,"E48.2.0.19"),sQuery(id+"F0.wireOp",EDGE,"E48.2.0.20"),sQuery(id+"F0.wireOp",EDGE,"E48.2.0.21"),sQuery(id+"F0.wireOp",EDGE,"E49.1.0.0"),sQuery(id+"F0.wireOp",EDGE,"E49.1.0.1"),sQuery(id+"F0.wireOp",EDGE,"E49.1.0.2"),sQuery(id+"F0.wireOp",EDGE,"E49.1.0.4"),sQuery(id+"F0.wireOp",EDGE,"E49.1.0.6"),sQuery(id+"F0.wireOp",EDGE,"E49.1.0.7"),sQuery(id+"F0.wireOp",EDGE,"E49.1.0.9"),sQuery(id+"F0.wireOp",EDGE,"E49.1.0.10"),sQuery(id+"F0.wireOp",EDGE,"E49.1.0.12"),sQuery(id+"F0.wireOp",EDGE,"E49.1.0.14"),sQuery(id+"F0.wireOp",EDGE,"E49.1.0.16"),sQuery(id+"F0.wireOp",EDGE,"E49.1.0.18"),sQuery(id+"F0.wireOp",EDGE,"E49.1.0.19"),sQuery(id+"F0.wireOp",EDGE,"E49.1.0.20"),sQuery(id+"F0.wireOp",EDGE,"E49.1.0.26"),sQuery(id+"F0.wireOp",EDGE,"E49.1.0.28"),sQuery(id+"F0.wireOp",EDGE,"E49.1.0.29"),sQuery(id+"F0.wireOp",EDGE,"E49.1.0.30"),sQuery(id+"F0.wireOp",EDGE,"E49.2.0.0"),sQuery(id+"F0.wireOp",EDGE,"E49.2.0.1"),sQuery(id+"F0.wireOp",EDGE,"E49.2.0.2"),sQuery(id+"F0.wireOp",EDGE,"E49.2.0.4"),sQuery(id+"F0.wireOp",EDGE,"E49.2.0.6"),sQuery(id+"F0.wireOp",EDGE,"E49.2.0.7"),sQuery(id+"F0.wireOp",EDGE,"E49.2.0.9"),sQuery(id+"F0.wireOp",EDGE,"E49.2.0.10"),sQuery(id+"F0.wireOp",EDGE,"E49.2.0.12"),sQuery(id+"F0.wireOp",EDGE,"E49.2.0.14"),sQuery(id+"F0.wireOp",EDGE,"E49.2.0.16"),sQuery(id+"F0.wireOp",EDGE,"E49.2.0.18"),sQuery(id+"F0.wireOp",EDGE,"E49.2.0.19"),sQuery(id+"F0.wireOp",EDGE,"E49.2.0.20"),sQuery(id+"F0.wireOp",EDGE,"E49.2.0.26"),sQuery(id+"F0.wireOp",EDGE,"E49.2.0.28"),sQuery(id+"F0.wireOp",EDGE,"E49.2.0.29"),sQuery(id+"F0.wireOp",EDGE,"E49.2.0.30")])],"isStart":false});
            extrude(context, id + "F2", {"entities" : qUnion([Q0]), "operationType" : NewBodyOperationType.ADD, "depth" : 10 * mm});
        }
        {
            var Q0;
            Q0=makeQuery(id+"F2.opExtrude","CAP_FACE",FACE,{"disambiguationData":[OSD([sQuery(id+"F0.wireOp",EDGE,"E0.bottom"),sQuery(id+"F0.wireOp",EDGE,"E0.top"),sQuery(id+"F0.wireOp",EDGE,"E0.left"),sQuery(id+"F0.wireOp",EDGE,"E0.right"),sQuery(id+"F0.wireOp",EDGE,"E5"),sQuery(id+"F0.wireOp",EDGE,"E6"),sQuery(id+"F0.wireOp",EDGE,"E7"),sQuery(id+"F0.wireOp",EDGE,"E10"),sQuery(id+"F0.wireOp",EDGE,"E11"),sQuery(id+"F0.wireOp",EDGE,"E12"),sQuery(id+"F0.wireOp",EDGE,"E13"),sQuery(id+"F0.wireOp",EDGE,"E14"),sQuery(id+"F0.wireOp",EDGE,"E15"),sQuery(id+"F0.wireOp",EDGE,"E16"),sQuery(id+"F0.wireOp",EDGE,"E17.bottom"),sQuery(id+"F0.wireOp",EDGE,"E17.top"),sQuery(id+"F0.wireOp",EDGE,"E17.left"),sQuery(id+"F0.wireOp",EDGE,"E17.right"),sQuery(id+"F0.wireOp",EDGE,"E18"),sQuery(id+"F0.wireOp",EDGE,"E19"),sQuery(id+"F0.wireOp",EDGE,"E21.bottom"),sQuery(id+"F0.wireOp",EDGE,"E21.top"),sQuery(id+"F0.wireOp",EDGE,"E21.left"),sQuery(id+"F0.wireOp",EDGE,"E21.right"),sQuery(id+"F0.wireOp",EDGE,"E23.bottom"),sQuery(id+"F0.wireOp",EDGE,"E23.top"),sQuery(id+"F0.wireOp",EDGE,"E24.left"),sQuery(id+"F0.wireOp",EDGE,"E24.right"),sQuery(id+"F0.wireOp",EDGE,"E25.left"),sQuery(id+"F0.wireOp",EDGE,"E25.right"),sQuery(id+"F0.wireOp",EDGE,"E26.trimOffspring"),sQuery(id+"F0.wireOp",EDGE,"E27.trimOffspring"),sQuery(id+"F0.wireOp",EDGE,"E28.trimOffspring"),sQuery(id+"F0.wireOp",EDGE,"E29.trimOffspring"),sQuery(id+"F0.wireOp",EDGE,"E30.trimOffspring"),sQuery(id+"F0.wireOp",EDGE,"E31.trimOffspring"),sQuery(id+"F0.wireOp",EDGE,"E32.trimOffspring"),sQuery(id+"F0.wireOp",EDGE,"E33.trimOffspring"),sQuery(id+"F0.wireOp",EDGE,"E22.bottom"),sQuery(id+"F0.wireOp",EDGE,"E22.top"),sQuery(id+"F0.wireOp",EDGE,"E22.left"),sQuery(id+"F0.wireOp",EDGE,"E22.right"),sQuery(id+"F0.wireOp",EDGE,"E35.bottom"),sQuery(id+"F0.wireOp",EDGE,"E35.top"),sQuery(id+"F0.wireOp",EDGE,"E36.left"),sQuery(id+"F0.wireOp",EDGE,"E36.right"),sQuery(id+"F0.wireOp",EDGE,"E37.left"),sQuery(id+"F0.wireOp",EDGE,"E37.right"),sQuery(id+"F0.wireOp",EDGE,"E38.trimOffspring"),sQuery(id+"F0.wireOp",EDGE,"E39.trimOffspring"),sQuery(id+"F0.wireOp",EDGE,"E40.trimOffspring"),sQuery(id+"F0.wireOp",EDGE,"E41.trimOffspring"),sQuery(id+"F0.wireOp",EDGE,"E42.trimOffspring"),sQuery(id+"F0.wireOp",EDGE,"E43.trimOffspring"),sQuery(id+"F0.wireOp",EDGE,"E44.trimOffspring"),sQuery(id+"F0.wireOp",EDGE,"E45.trimOffspring"),sQuery(id+"F0.wireOp",EDGE,"E46.bottom"),sQuery(id+"F0.wireOp",EDGE,"E46.top"),sQuery(id+"F0.wireOp",EDGE,"E46.left"),sQuery(id+"F0.wireOp",EDGE,"E46.right"),sQuery(id+"F0.wireOp",EDGE,"E47.bottom"),sQuery(id+"F0.wireOp",EDGE,"E47.top"),sQuery(id+"F0.wireOp",EDGE,"E47.left"),sQuery(id+"F0.wireOp",EDGE,"E47.right"),sQuery(id+"F0.wireOp",EDGE,"E48.1.0.0"),sQuery(id+"F0.wireOp",EDGE,"E48.1.0.2"),sQuery(id+"F0.wireOp",EDGE,"E48.1.0.3"),sQuery(id+"F0.wireOp",EDGE,"E48.1.0.5"),sQuery(id+"F0.wireOp",EDGE,"E48.1.0.6"),sQuery(id+"F0.wireOp",EDGE,"E48.1.0.7"),sQuery(id+"F0.wireOp",EDGE,"E48.1.0.8"),sQuery(id+"F0.wireOp",EDGE,"E48.1.0.9"),sQuery(id+"F0.wireOp",EDGE,"E48.1.0.12"),sQuery(id+"F0.wireOp",EDGE,"E48.1.0.13"),sQuery(id+"F0.wireOp",EDGE,"E48.1.0.14"),sQuery(id+"F0.wireOp",EDGE,"E48.1.0.15"),sQuery(id+"F0.wireOp",EDGE,"E48.1.0.16"),sQuery(id+"F0.wireOp",EDGE,"E48.1.0.17"),sQuery(id+"F0.wireOp",EDGE,"E48.1.0.18"),sQuery(id+"F0.wireOp",EDGE,"E48.1.0.19"),sQuery(id+"F0.wireOp",EDGE,"E48.1.0.20"),sQuery(id+"F0.wireOp",EDGE,"E48.1.0.21"),sQuery(id+"F0.wireOp",EDGE,"E48.2.0.0"),sQuery(id+"F0.wireOp",EDGE,"E48.2.0.2"),sQuery(id+"F0.wireOp",EDGE,"E48.2.0.3"),sQuery(id+"F0.wireOp",EDGE,"E48.2.0.5"),sQuery(id+"F0.wireOp",EDGE,"E48.2.0.6"),sQuery(id+"F0.wireOp",EDGE,"E48.2.0.7"),sQuery(id+"F0.wireOp",EDGE,"E48.2.0.8"),sQuery(id+"F0.wireOp",EDGE,"E48.2.0.9"),sQuery(id+"F0.wireOp",EDGE,"E48.2.0.12"),sQuery(id+"F0.wireOp",EDGE,"E48.2.0.13"),sQuery(id+"F0.wireOp",EDGE,"E48.2.0.14"),sQuery(id+"F0.wireOp",EDGE,"E48.2.0.15"),sQuery(id+"F0.wireOp",EDGE,"E48.2.0.16"),sQuery(id+"F0.wireOp",EDGE,"E48.2.0.17"),sQuery(id+"F0.wireOp",EDGE,"E48.2.0.18"),sQuery(id+"F0.wireOp",EDGE,"E48.2.0.19"),sQuery(id+"F0.wireOp",EDGE,"E48.2.0.20"),sQuery(id+"F0.wireOp",EDGE,"E48.2.0.21"),sQuery(id+"F0.wireOp",EDGE,"E49.1.0.0"),sQuery(id+"F0.wireOp",EDGE,"E49.1.0.1"),sQuery(id+"F0.wireOp",EDGE,"E49.1.0.2"),sQuery(id+"F0.wireOp",EDGE,"E49.1.0.4"),sQuery(id+"F0.wireOp",EDGE,"E49.1.0.6"),sQuery(id+"F0.wireOp",EDGE,"E49.1.0.7"),sQuery(id+"F0.wireOp",EDGE,"E49.1.0.9"),sQuery(id+"F0.wireOp",EDGE,"E49.1.0.10"),sQuery(id+"F0.wireOp",EDGE,"E49.1.0.12"),sQuery(id+"F0.wireOp",EDGE,"E49.1.0.14"),sQuery(id+"F0.wireOp",EDGE,"E49.1.0.16"),sQuery(id+"F0.wireOp",EDGE,"E49.1.0.18"),sQuery(id+"F0.wireOp",EDGE,"E49.1.0.19"),sQuery(id+"F0.wireOp",EDGE,"E49.1.0.20"),sQuery(id+"F0.wireOp",EDGE,"E49.1.0.26"),sQuery(id+"F0.wireOp",EDGE,"E49.1.0.28"),sQuery(id+"F0.wireOp",EDGE,"E49.1.0.29"),sQuery(id+"F0.wireOp",EDGE,"E49.1.0.30"),sQuery(id+"F0.wireOp",EDGE,"E49.2.0.0"),sQuery(id+"F0.wireOp",EDGE,"E49.2.0.1"),sQuery(id+"F0.wireOp",EDGE,"E49.2.0.2"),sQuery(id+"F0.wireOp",EDGE,"E49.2.0.4"),sQuery(id+"F0.wireOp",EDGE,"E49.2.0.6"),sQuery(id+"F0.wireOp",EDGE,"E49.2.0.7"),sQuery(id+"F0.wireOp",EDGE,"E49.2.0.9"),sQuery(id+"F0.wireOp",EDGE,"E49.2.0.10"),sQuery(id+"F0.wireOp",EDGE,"E49.2.0.12"),sQuery(id+"F0.wireOp",EDGE,"E49.2.0.14"),sQuery(id+"F0.wireOp",EDGE,"E49.2.0.16"),sQuery(id+"F0.wireOp",EDGE,"E49.2.0.18"),sQuery(id+"F0.wireOp",EDGE,"E49.2.0.19"),sQuery(id+"F0.wireOp",EDGE,"E49.2.0.20"),sQuery(id+"F0.wireOp",EDGE,"E49.2.0.26"),sQuery(id+"F0.wireOp",EDGE,"E49.2.0.28"),sQuery(id+"F0.wireOp",EDGE,"E49.2.0.29"),sQuery(id+"F0.wireOp",EDGE,"E49.2.0.30")])],"isStart":false});
            var sketch = newSketch(context, id + "F3", { "sketchPlane" : qUnion([Q0])});
            skPoint(sketch, "E52.0", {"position": v(-111.5, 3.96) * mm});
            skLineSegment(sketch, "E53.bottom", {"start": v(-102.5, -5.04) * mm, "end": v(-120.5, -5.04) * mm});
            skLineSegment(sketch, "E53.top", {"start": v(-102.5, 12.96) * mm, "end": v(-120.5, 12.96) * mm});
            skLineSegment(sketch, "E53.left", {"start": v(-102.5, -5.04) * mm, "end": v(-102.5, 12.96) * mm});
            skLineSegment(sketch, "E53.right", {"start": v(-120.5, -5.04) * mm, "end": v(-120.5, 12.96) * mm});
            skPoint(sketch, "E54.0", {"position": v(-111.5, -21.04) * mm});
            skLineSegment(sketch, "E55.bottom", {"start": v(-102.5, -30.04) * mm, "end": v(-120.5, -30.04) * mm});
            skLineSegment(sketch, "E55.top", {"start": v(-102.5, -12.04) * mm, "end": v(-120.5, -12.04) * mm});
            skLineSegment(sketch, "E55.left", {"start": v(-102.5, -30.04) * mm, "end": v(-102.5, -12.04) * mm});
            skLineSegment(sketch, "E55.right", {"start": v(-120.5, -30.04) * mm, "end": v(-120.5, -12.04) * mm});
            skLineSegment(sketch, "E56.1.0.0", {"start": v(-76.5, -5.04) * mm, "end": v(-94.5, -5.04) * mm});
            skLineSegment(sketch, "E56.1.0.1", {"start": v(-76.5, -12.04) * mm, "end": v(-94.5, -12.04) * mm});
            skLineSegment(sketch, "E56.1.0.2", {"start": v(-94.5, -5.04) * mm, "end": v(-94.5, 12.96) * mm});
            skPoint(sketch, "E56.1.0.3", {"position": v(-85.5, 3.96) * mm});
            skLineSegment(sketch, "E56.1.0.4", {"start": v(-76.5, -30.04) * mm, "end": v(-76.5, -12.04) * mm});
            skLineSegment(sketch, "E56.1.0.5", {"start": v(-76.5, -30.04) * mm, "end": v(-94.5, -30.04) * mm});
            skPoint(sketch, "E56.1.0.6", {"position": v(-85.5, -21.04) * mm});
            skLineSegment(sketch, "E56.1.0.7", {"start": v(-76.5, -5.04) * mm, "end": v(-76.5, 12.96) * mm});
            skLineSegment(sketch, "E56.1.0.8", {"start": v(-76.5, 12.96) * mm, "end": v(-94.5, 12.96) * mm});
            skLineSegment(sketch, "E56.1.0.9", {"start": v(-94.5, -30.04) * mm, "end": v(-94.5, -12.04) * mm});
            skPoint(sketch, "E56.1.0.10", {"position": v(-85.5, 3.96) * mm});
            skPoint(sketch, "E56.1.0.11", {"position": v(-85.5, -21.04) * mm});
            skLineSegment(sketch, "E56.2.0.0", {"start": v(-50.5, -5.04) * mm, "end": v(-68.5, -5.04) * mm});
            skLineSegment(sketch, "E56.2.0.1", {"start": v(-50.5, -12.04) * mm, "end": v(-68.5, -12.04) * mm});
            skLineSegment(sketch, "E56.2.0.2", {"start": v(-68.5, -5.04) * mm, "end": v(-68.5, 12.96) * mm});
            skPoint(sketch, "E56.2.0.3", {"position": v(-59.5, 3.96) * mm});
            skLineSegment(sketch, "E56.2.0.4", {"start": v(-50.5, -30.04) * mm, "end": v(-50.5, -12.04) * mm});
            skLineSegment(sketch, "E56.2.0.5", {"start": v(-50.5, -30.04) * mm, "end": v(-68.5, -30.04) * mm});
            skPoint(sketch, "E56.2.0.6", {"position": v(-59.5, -21.04) * mm});
            skLineSegment(sketch, "E56.2.0.7", {"start": v(-50.5, -5.04) * mm, "end": v(-50.5, 12.96) * mm});
            skLineSegment(sketch, "E56.2.0.8", {"start": v(-50.5, 12.96) * mm, "end": v(-68.5, 12.96) * mm});
            skLineSegment(sketch, "E56.2.0.9", {"start": v(-68.5, -30.04) * mm, "end": v(-68.5, -12.04) * mm});
            skPoint(sketch, "E56.2.0.10", {"position": v(-59.5, 3.96) * mm});
            skPoint(sketch, "E56.2.0.11", {"position": v(-59.5, -21.04) * mm});
            skLineSegment(sketch, "E56.direction1", {"start": v(-120.5, -30.04) * mm, "end": v(-94.5, -30.04) * mm, "construction": true});
            skSolve(sketch);
        }
        {
            var Q0;
            Q0=qSketchRegion(id+"F3",true);
            extrude(context, id + "F4", {"entities" : qUnion([Q0]), "operationType" : NewBodyOperationType.REMOVE, "oppositeDirection" : true, "depth" : 10 * mm});
        }
        {
            var Q0;
            Q0=makeQuery(id+"F2.opExtrude","CAP_FACE",FACE,{"disambiguationData":[OSD([sQuery(id+"F0.wireOp",EDGE,"E0.bottom"),sQuery(id+"F0.wireOp",EDGE,"E0.top"),sQuery(id+"F0.wireOp",EDGE,"E0.left"),sQuery(id+"F0.wireOp",EDGE,"E0.right"),sQuery(id+"F0.wireOp",EDGE,"E5"),sQuery(id+"F0.wireOp",EDGE,"E6"),sQuery(id+"F0.wireOp",EDGE,"E7"),sQuery(id+"F0.wireOp",EDGE,"E10"),sQuery(id+"F0.wireOp",EDGE,"E11"),sQuery(id+"F0.wireOp",EDGE,"E12"),sQuery(id+"F0.wireOp",EDGE,"E13"),sQuery(id+"F0.wireOp",EDGE,"E14"),sQuery(id+"F0.wireOp",EDGE,"E15"),sQuery(id+"F0.wireOp",EDGE,"E16"),sQuery(id+"F0.wireOp",EDGE,"E17.bottom"),sQuery(id+"F0.wireOp",EDGE,"E17.top"),sQuery(id+"F0.wireOp",EDGE,"E17.left"),sQuery(id+"F0.wireOp",EDGE,"E17.right"),sQuery(id+"F0.wireOp",EDGE,"E18"),sQuery(id+"F0.wireOp",EDGE,"E19"),sQuery(id+"F0.wireOp",EDGE,"E21.bottom"),sQuery(id+"F0.wireOp",EDGE,"E21.top"),sQuery(id+"F0.wireOp",EDGE,"E21.left"),sQuery(id+"F0.wireOp",EDGE,"E21.right"),sQuery(id+"F0.wireOp",EDGE,"E23.bottom"),sQuery(id+"F0.wireOp",EDGE,"E23.top"),sQuery(id+"F0.wireOp",EDGE,"E24.left"),sQuery(id+"F0.wireOp",EDGE,"E24.right"),sQuery(id+"F0.wireOp",EDGE,"E25.left"),sQuery(id+"F0.wireOp",EDGE,"E25.right"),sQuery(id+"F0.wireOp",EDGE,"E26.trimOffspring"),sQuery(id+"F0.wireOp",EDGE,"E27.trimOffspring"),sQuery(id+"F0.wireOp",EDGE,"E28.trimOffspring"),sQuery(id+"F0.wireOp",EDGE,"E29.trimOffspring"),sQuery(id+"F0.wireOp",EDGE,"E30.trimOffspring"),sQuery(id+"F0.wireOp",EDGE,"E31.trimOffspring"),sQuery(id+"F0.wireOp",EDGE,"E32.trimOffspring"),sQuery(id+"F0.wireOp",EDGE,"E33.trimOffspring"),sQuery(id+"F0.wireOp",EDGE,"E22.bottom"),sQuery(id+"F0.wireOp",EDGE,"E22.top"),sQuery(id+"F0.wireOp",EDGE,"E22.left"),sQuery(id+"F0.wireOp",EDGE,"E22.right"),sQuery(id+"F0.wireOp",EDGE,"E35.bottom"),sQuery(id+"F0.wireOp",EDGE,"E35.top"),sQuery(id+"F0.wireOp",EDGE,"E36.left"),sQuery(id+"F0.wireOp",EDGE,"E36.right"),sQuery(id+"F0.wireOp",EDGE,"E37.left"),sQuery(id+"F0.wireOp",EDGE,"E37.right"),sQuery(id+"F0.wireOp",EDGE,"E38.trimOffspring"),sQuery(id+"F0.wireOp",EDGE,"E39.trimOffspring"),sQuery(id+"F0.wireOp",EDGE,"E40.trimOffspring"),sQuery(id+"F0.wireOp",EDGE,"E41.trimOffspring"),sQuery(id+"F0.wireOp",EDGE,"E42.trimOffspring"),sQuery(id+"F0.wireOp",EDGE,"E43.trimOffspring"),sQuery(id+"F0.wireOp",EDGE,"E44.trimOffspring"),sQuery(id+"F0.wireOp",EDGE,"E45.trimOffspring"),sQuery(id+"F0.wireOp",EDGE,"E46.bottom"),sQuery(id+"F0.wireOp",EDGE,"E46.top"),sQuery(id+"F0.wireOp",EDGE,"E46.left"),sQuery(id+"F0.wireOp",EDGE,"E46.right"),sQuery(id+"F0.wireOp",EDGE,"E47.bottom"),sQuery(id+"F0.wireOp",EDGE,"E47.top"),sQuery(id+"F0.wireOp",EDGE,"E47.left"),sQuery(id+"F0.wireOp",EDGE,"E47.right"),sQuery(id+"F0.wireOp",EDGE,"E48.1.0.0"),sQuery(id+"F0.wireOp",EDGE,"E48.1.0.2"),sQuery(id+"F0.wireOp",EDGE,"E48.1.0.3"),sQuery(id+"F0.wireOp",EDGE,"E48.1.0.5"),sQuery(id+"F0.wireOp",EDGE,"E48.1.0.6"),sQuery(id+"F0.wireOp",EDGE,"E48.1.0.7"),sQuery(id+"F0.wireOp",EDGE,"E48.1.0.8"),sQuery(id+"F0.wireOp",EDGE,"E48.1.0.9"),sQuery(id+"F0.wireOp",EDGE,"E48.1.0.12"),sQuery(id+"F0.wireOp",EDGE,"E48.1.0.13"),sQuery(id+"F0.wireOp",EDGE,"E48.1.0.14"),sQuery(id+"F0.wireOp",EDGE,"E48.1.0.15"),sQuery(id+"F0.wireOp",EDGE,"E48.1.0.16"),sQuery(id+"F0.wireOp",EDGE,"E48.1.0.17"),sQuery(id+"F0.wireOp",EDGE,"E48.1.0.18"),sQuery(id+"F0.wireOp",EDGE,"E48.1.0.19"),sQuery(id+"F0.wireOp",EDGE,"E48.1.0.20"),sQuery(id+"F0.wireOp",EDGE,"E48.1.0.21"),sQuery(id+"F0.wireOp",EDGE,"E48.2.0.0"),sQuery(id+"F0.wireOp",EDGE,"E48.2.0.2"),sQuery(id+"F0.wireOp",EDGE,"E48.2.0.3"),sQuery(id+"F0.wireOp",EDGE,"E48.2.0.5"),sQuery(id+"F0.wireOp",EDGE,"E48.2.0.6"),sQuery(id+"F0.wireOp",EDGE,"E48.2.0.7"),sQuery(id+"F0.wireOp",EDGE,"E48.2.0.8"),sQuery(id+"F0.wireOp",EDGE,"E48.2.0.9"),sQuery(id+"F0.wireOp",EDGE,"E48.2.0.12"),sQuery(id+"F0.wireOp",EDGE,"E48.2.0.13"),sQuery(id+"F0.wireOp",EDGE,"E48.2.0.14"),sQuery(id+"F0.wireOp",EDGE,"E48.2.0.15"),sQuery(id+"F0.wireOp",EDGE,"E48.2.0.16"),sQuery(id+"F0.wireOp",EDGE,"E48.2.0.17"),sQuery(id+"F0.wireOp",EDGE,"E48.2.0.18"),sQuery(id+"F0.wireOp",EDGE,"E48.2.0.19"),sQuery(id+"F0.wireOp",EDGE,"E48.2.0.20"),sQuery(id+"F0.wireOp",EDGE,"E48.2.0.21"),sQuery(id+"F0.wireOp",EDGE,"E49.1.0.0"),sQuery(id+"F0.wireOp",EDGE,"E49.1.0.1"),sQuery(id+"F0.wireOp",EDGE,"E49.1.0.2"),sQuery(id+"F0.wireOp",EDGE,"E49.1.0.4"),sQuery(id+"F0.wireOp",EDGE,"E49.1.0.6"),sQuery(id+"F0.wireOp",EDGE,"E49.1.0.7"),sQuery(id+"F0.wireOp",EDGE,"E49.1.0.9"),sQuery(id+"F0.wireOp",EDGE,"E49.1.0.10"),sQuery(id+"F0.wireOp",EDGE,"E49.1.0.12"),sQuery(id+"F0.wireOp",EDGE,"E49.1.0.14"),sQuery(id+"F0.wireOp",EDGE,"E49.1.0.16"),sQuery(id+"F0.wireOp",EDGE,"E49.1.0.18"),sQuery(id+"F0.wireOp",EDGE,"E49.1.0.19"),sQuery(id+"F0.wireOp",EDGE,"E49.1.0.20"),sQuery(id+"F0.wireOp",EDGE,"E49.1.0.26"),sQuery(id+"F0.wireOp",EDGE,"E49.1.0.28"),sQuery(id+"F0.wireOp",EDGE,"E49.1.0.29"),sQuery(id+"F0.wireOp",EDGE,"E49.1.0.30"),sQuery(id+"F0.wireOp",EDGE,"E49.2.0.0"),sQuery(id+"F0.wireOp",EDGE,"E49.2.0.1"),sQuery(id+"F0.wireOp",EDGE,"E49.2.0.2"),sQuery(id+"F0.wireOp",EDGE,"E49.2.0.4"),sQuery(id+"F0.wireOp",EDGE,"E49.2.0.6"),sQuery(id+"F0.wireOp",EDGE,"E49.2.0.7"),sQuery(id+"F0.wireOp",EDGE,"E49.2.0.9"),sQuery(id+"F0.wireOp",EDGE,"E49.2.0.10"),sQuery(id+"F0.wireOp",EDGE,"E49.2.0.12"),sQuery(id+"F0.wireOp",EDGE,"E49.2.0.14"),sQuery(id+"F0.wireOp",EDGE,"E49.2.0.16"),sQuery(id+"F0.wireOp",EDGE,"E49.2.0.18"),sQuery(id+"F0.wireOp",EDGE,"E49.2.0.19"),sQuery(id+"F0.wireOp",EDGE,"E49.2.0.20"),sQuery(id+"F0.wireOp",EDGE,"E49.2.0.26"),sQuery(id+"F0.wireOp",EDGE,"E49.2.0.28"),sQuery(id+"F0.wireOp",EDGE,"E49.2.0.29"),sQuery(id+"F0.wireOp",EDGE,"E49.2.0.30")])],"isStart":false});
            var sketch = newSketch(context, id + "F5", { "sketchPlane" : qUnion([Q0])});
            skPoint(sketch, "E57.0", {"position": v(-111.5, 3.96) * mm});
            skPoint(sketch, "E57.1", {"position": v(-111.5, -21.04) * mm});
            skLineSegment(sketch, "E58.bottom", {"start": v(-122.5, 8.96) * mm, "end": v(-120.5, 8.96) * mm});
            skLineSegment(sketch, "E58.top", {"start": v(-122.5, -1.04) * mm, "end": v(-120.5, -1.04) * mm});
            skLineSegment(sketch, "E58.left", {"start": v(-122.5, 8.96) * mm, "end": v(-122.5, -1.04) * mm});
            skLineSegment(sketch, "E58.right", {"start": v(-120.5, 8.96) * mm, "end": v(-120.5, -1.04) * mm});
            skPoint(sketch, "E59", {"position": v(-121.5, 3.96) * mm});
            skPoint(sketch, "E59.positionSnap0", {"position": v(-121.5, 8.96) * mm});
            skPoint(sketch, "E59.positionSnap1", {"position": v(-122.5, 3.96) * mm});
            skPoint(sketch, "E60.firstSnap0", {"position": v(-102.5, 3.96) * mm});
            skLineSegment(sketch, "E60.bottom", {"start": v(-102.5, 8.96) * mm, "end": v(-100.5, 8.96) * mm});
            skLineSegment(sketch, "E60.top", {"start": v(-102.5, -1.04) * mm, "end": v(-100.5, -1.04) * mm});
            skLineSegment(sketch, "E60.left", {"start": v(-102.5, 8.96) * mm, "end": v(-102.5, -1.04) * mm});
            skLineSegment(sketch, "E60.right", {"start": v(-100.5, 8.96) * mm, "end": v(-100.5, -1.04) * mm});
            skLineSegment(sketch, "E61.1.0.0", {"start": v(-76.5, 8.96) * mm, "end": v(-76.5, -1.04) * mm});
            skLineSegment(sketch, "E61.1.0.1", {"start": v(-74.5, 8.96) * mm, "end": v(-74.5, -1.04) * mm});
            skPoint(sketch, "E61.1.0.2", {"position": v(-85.5, 3.96) * mm});
            skPoint(sketch, "E61.1.0.3", {"position": v(-96.5, 3.96) * mm});
            skPoint(sketch, "E61.1.0.4", {"position": v(-95.5, 3.96) * mm});
            skLineSegment(sketch, "E61.1.0.5", {"start": v(-96.5, -1.04) * mm, "end": v(-94.5, -1.04) * mm});
            skLineSegment(sketch, "E61.1.0.6", {"start": v(-76.5, 8.96) * mm, "end": v(-74.5, 8.96) * mm});
            skPoint(sketch, "E61.1.0.7", {"position": v(-76.5, 3.96) * mm});
            skPoint(sketch, "E61.1.0.8", {"position": v(-95.5, 8.96) * mm});
            skLineSegment(sketch, "E61.1.0.9", {"start": v(-94.5, 8.96) * mm, "end": v(-94.5, -1.04) * mm});
            skLineSegment(sketch, "E61.1.0.10", {"start": v(-76.5, -1.04) * mm, "end": v(-74.5, -1.04) * mm});
            skLineSegment(sketch, "E61.1.0.11", {"start": v(-96.5, 8.96) * mm, "end": v(-96.5, -1.04) * mm});
            skLineSegment(sketch, "E61.1.0.12", {"start": v(-96.5, 8.96) * mm, "end": v(-94.5, 8.96) * mm});
            skLineSegment(sketch, "E61.2.0.0", {"start": v(-50.5, 8.96) * mm, "end": v(-50.5, -1.04) * mm});
            skLineSegment(sketch, "E61.2.0.1", {"start": v(-48.5, 8.96) * mm, "end": v(-48.5, -1.04) * mm});
            skPoint(sketch, "E61.2.0.2", {"position": v(-59.5, 3.96) * mm});
            skPoint(sketch, "E61.2.0.3", {"position": v(-70.5, 3.96) * mm});
            skPoint(sketch, "E61.2.0.4", {"position": v(-69.5, 3.96) * mm});
            skLineSegment(sketch, "E61.2.0.5", {"start": v(-70.5, -1.04) * mm, "end": v(-68.5, -1.04) * mm});
            skLineSegment(sketch, "E61.2.0.6", {"start": v(-50.5, 8.96) * mm, "end": v(-48.5, 8.96) * mm});
            skPoint(sketch, "E61.2.0.7", {"position": v(-50.5, 3.96) * mm});
            skPoint(sketch, "E61.2.0.8", {"position": v(-69.5, 8.96) * mm});
            skLineSegment(sketch, "E61.2.0.9", {"start": v(-68.5, 8.96) * mm, "end": v(-68.5, -1.04) * mm});
            skLineSegment(sketch, "E61.2.0.10", {"start": v(-50.5, -1.04) * mm, "end": v(-48.5, -1.04) * mm});
            skLineSegment(sketch, "E61.2.0.11", {"start": v(-70.5, 8.96) * mm, "end": v(-70.5, -1.04) * mm});
            skLineSegment(sketch, "E61.2.0.12", {"start": v(-70.5, 8.96) * mm, "end": v(-68.5, 8.96) * mm});
            skLineSegment(sketch, "E61.direction1", {"start": v(-122.5, -1.04) * mm, "end": v(-96.5, -1.04) * mm, "construction": true});
            skLineSegment(sketch, "E62.bottom", {"start": v(-120.5, -16.04) * mm, "end": v(-122.5, -16.04) * mm});
            skLineSegment(sketch, "E62.top", {"start": v(-120.5, -26.04) * mm, "end": v(-122.5, -26.04) * mm});
            skLineSegment(sketch, "E62.left", {"start": v(-120.5, -16.04) * mm, "end": v(-120.5, -26.04) * mm});
            skLineSegment(sketch, "E62.right", {"start": v(-122.5, -16.04) * mm, "end": v(-122.5, -26.04) * mm});
            skLineSegment(sketch, "E63.bottom", {"start": v(-102.5, -16.04) * mm, "end": v(-100.5, -16.04) * mm});
            skLineSegment(sketch, "E63.top", {"start": v(-102.5, -26.04) * mm, "end": v(-100.5, -26.04) * mm});
            skLineSegment(sketch, "E63.left", {"start": v(-102.5, -16.04) * mm, "end": v(-102.5, -26.04) * mm});
            skLineSegment(sketch, "E63.right", {"start": v(-100.5, -16.04) * mm, "end": v(-100.5, -26.04) * mm});
            skLineSegment(sketch, "E64.1.0.0", {"start": v(-94.5, -16.04) * mm, "end": v(-94.5, -26.04) * mm});
            skPoint(sketch, "E64.1.0.1", {"position": v(-85.5, -21.04) * mm});
            skLineSegment(sketch, "E64.1.0.2", {"start": v(-76.5, -26.04) * mm, "end": v(-74.5, -26.04) * mm});
            skLineSegment(sketch, "E64.1.0.3", {"start": v(-74.5, -16.04) * mm, "end": v(-74.5, -26.04) * mm});
            skLineSegment(sketch, "E64.1.0.4", {"start": v(-94.5, -16.04) * mm, "end": v(-96.5, -16.04) * mm});
            skLineSegment(sketch, "E64.1.0.5", {"start": v(-76.5, -16.04) * mm, "end": v(-76.5, -26.04) * mm});
            skLineSegment(sketch, "E64.1.0.6", {"start": v(-94.5, -26.04) * mm, "end": v(-96.5, -26.04) * mm});
            skLineSegment(sketch, "E64.1.0.7", {"start": v(-76.5, -16.04) * mm, "end": v(-74.5, -16.04) * mm});
            skLineSegment(sketch, "E64.1.0.8", {"start": v(-96.5, -16.04) * mm, "end": v(-96.5, -26.04) * mm});
            skLineSegment(sketch, "E64.2.0.0", {"start": v(-68.5, -16.04) * mm, "end": v(-68.5, -26.04) * mm});
            skPoint(sketch, "E64.2.0.1", {"position": v(-59.5, -21.04) * mm});
            skLineSegment(sketch, "E64.2.0.2", {"start": v(-50.5, -26.04) * mm, "end": v(-48.5, -26.04) * mm});
            skLineSegment(sketch, "E64.2.0.3", {"start": v(-48.5, -16.04) * mm, "end": v(-48.5, -26.04) * mm});
            skLineSegment(sketch, "E64.2.0.4", {"start": v(-68.5, -16.04) * mm, "end": v(-70.5, -16.04) * mm});
            skLineSegment(sketch, "E64.2.0.5", {"start": v(-50.5, -16.04) * mm, "end": v(-50.5, -26.04) * mm});
            skLineSegment(sketch, "E64.2.0.6", {"start": v(-68.5, -26.04) * mm, "end": v(-70.5, -26.04) * mm});
            skLineSegment(sketch, "E64.2.0.7", {"start": v(-50.5, -16.04) * mm, "end": v(-48.5, -16.04) * mm});
            skLineSegment(sketch, "E64.2.0.8", {"start": v(-70.5, -16.04) * mm, "end": v(-70.5, -26.04) * mm});
            skLineSegment(sketch, "E64.direction1", {"start": v(-122.5, -26.04) * mm, "end": v(-96.5, -26.04) * mm, "construction": true});
            skPoint(sketch, "E65", {"position": v(-121.5, -21.04) * mm});
            skPoint(sketch, "E65.positionSnap0", {"position": v(-121.5, -16.04) * mm});
            skPoint(sketch, "E65.positionSnap1", {"position": v(-122.5, -21.04) * mm});
            skSolve(sketch);
        }
        {
            var Q0;
            Q0=qSketchRegion(id+"F5",true);
            extrude(context, id + "F6", {"entities" : qUnion([Q0]), "operationType" : NewBodyOperationType.REMOVE, "oppositeDirection" : true, "depth" : 10 * mm});
        }
        {
            var Q0;
            Q0=qCreatedBy(makeId("Top.planeOp"),FACE);
            var sketch = newSketch(context, id + "F7", { "sketchPlane" : qUnion([Q0])});
            skLineSegment(sketch, "E66.bottom", {"start": v(-106.79, 77.03) * mm, "end": v(-126.79, 77.03) * mm});
            skLineSegment(sketch, "E66.top", {"start": v(-106.79, 97.03) * mm, "end": v(-126.79, 97.03) * mm});
            skLineSegment(sketch, "E66.left", {"start": v(-106.79, 77.03) * mm, "end": v(-106.79, 97.03) * mm});
            skLineSegment(sketch, "E66.right", {"start": v(-126.79, 77.03) * mm, "end": v(-126.79, 97.03) * mm});
            skPoint(sketch, "E66.middle", {"position": v(-116.79, 87.03) * mm});
            skLineSegment(sketch, "E67.bottom", {"start": v(-105.79, 82.03) * mm, "end": v(-107.79, 82.03) * mm});
            skLineSegment(sketch, "E67.top", {"start": v(-105.79, 92.03) * mm, "end": v(-107.79, 92.03) * mm});
            skLineSegment(sketch, "E67.left", {"start": v(-105.79, 82.03) * mm, "end": v(-105.79, 92.03) * mm});
            skLineSegment(sketch, "E67.right", {"start": v(-107.79, 82.03) * mm, "end": v(-107.79, 92.03) * mm});
            skPoint(sketch, "E67.middle", {"position": v(-106.79, 87.03) * mm});
            skLineSegment(sketch, "E68.bottom", {"start": v(-125.79, 82.03) * mm, "end": v(-127.79, 82.03) * mm});
            skLineSegment(sketch, "E68.top", {"start": v(-125.79, 92.03) * mm, "end": v(-127.79, 92.03) * mm});
            skLineSegment(sketch, "E68.left", {"start": v(-125.79, 82.03) * mm, "end": v(-125.79, 92.03) * mm});
            skLineSegment(sketch, "E68.right", {"start": v(-127.79, 82.03) * mm, "end": v(-127.79, 92.03) * mm});
            skPoint(sketch, "E68.middle", {"position": v(-126.79, 87.03) * mm});
            skLineSegment(sketch, "E69.bottom", {"start": v(-107.79, 78.03) * mm, "end": v(-125.79, 78.03) * mm});
            skLineSegment(sketch, "E69.top", {"start": v(-107.79, 96.03) * mm, "end": v(-125.79, 96.03) * mm});
            skLineSegment(sketch, "E69.left", {"start": v(-107.79, 78.03) * mm, "end": v(-107.79, 96.03) * mm});
            skLineSegment(sketch, "E69.right", {"start": v(-125.79, 78.03) * mm, "end": v(-125.79, 96.03) * mm});
            skLineSegment(sketch, "E70.bottom", {"start": v(-107.79, 86.53) * mm, "end": v(-125.79, 86.53) * mm});
            skLineSegment(sketch, "E70.top", {"start": v(-107.79, 87.53) * mm, "end": v(-125.79, 87.53) * mm});
            skLineSegment(sketch, "E70.left", {"start": v(-107.79, 86.53) * mm, "end": v(-107.79, 87.53) * mm});
            skLineSegment(sketch, "E70.right", {"start": v(-125.79, 86.53) * mm, "end": v(-125.79, 87.53) * mm});
            skLineSegment(sketch, "E71.bottom", {"start": v(-115.79, 85.78) * mm, "end": v(-117.79, 85.78) * mm, "construction": true});
            skLineSegment(sketch, "E71.top", {"start": v(-115.79, 88.28) * mm, "end": v(-117.79, 88.28) * mm, "construction": true});
            skLineSegment(sketch, "E71.left", {"start": v(-115.79, 85.78) * mm, "end": v(-115.79, 88.28) * mm, "construction": true});
            skLineSegment(sketch, "E71.right", {"start": v(-117.79, 85.78) * mm, "end": v(-117.79, 88.28) * mm, "construction": true});
            skLineSegment(sketch, "E72.bottom", {"start": v(-110.82, 38.4) * mm, "end": v(-132.62, 38.4) * mm});
            skLineSegment(sketch, "E72.top", {"start": v(-110.82, 60.2) * mm, "end": v(-132.62, 60.2) * mm});
            skLineSegment(sketch, "E72.left", {"start": v(-110.82, 38.4) * mm, "end": v(-110.82, 60.2) * mm});
            skLineSegment(sketch, "E72.right", {"start": v(-132.62, 38.4) * mm, "end": v(-132.62, 60.2) * mm});
            skPoint(sketch, "E72.middle", {"position": v(-121.72, 49.3) * mm});
            skLineSegment(sketch, "E73.bottom", {"start": v(-110.82, 44.4) * mm, "end": v(-112.62, 44.4) * mm});
            skLineSegment(sketch, "E73.top", {"start": v(-110.82, 54.2) * mm, "end": v(-112.62, 54.2) * mm});
            skLineSegment(sketch, "E73.left", {"start": v(-110.82, 44.4) * mm, "end": v(-110.82, 54.2) * mm});
            skLineSegment(sketch, "E73.right", {"start": v(-112.62, 44.4) * mm, "end": v(-112.62, 54.2) * mm});
            skPoint(sketch, "E73.middle", {"position": v(-111.72, 49.3) * mm});
            skLineSegment(sketch, "E74.bottom", {"start": v(-130.82, 44.4) * mm, "end": v(-132.62, 44.4) * mm});
            skLineSegment(sketch, "E74.top", {"start": v(-130.82, 54.2) * mm, "end": v(-132.62, 54.2) * mm});
            skLineSegment(sketch, "E74.left", {"start": v(-130.82, 44.4) * mm, "end": v(-130.82, 54.2) * mm});
            skLineSegment(sketch, "E74.right", {"start": v(-132.62, 44.4) * mm, "end": v(-132.62, 54.2) * mm});
            skPoint(sketch, "E74.middle", {"position": v(-131.72, 49.3) * mm});
            skLineSegment(sketch, "E75.bottom", {"start": v(-112.62, 40.2) * mm, "end": v(-130.82, 40.2) * mm});
            skLineSegment(sketch, "E75.top", {"start": v(-112.62, 58.4) * mm, "end": v(-130.82, 58.4) * mm});
            skLineSegment(sketch, "E75.left", {"start": v(-112.62, 40.2) * mm, "end": v(-112.62, 58.4) * mm});
            skLineSegment(sketch, "E75.right", {"start": v(-130.82, 40.2) * mm, "end": v(-130.82, 58.4) * mm});
            skSolve(sketch);
        }
        {
            var Q0;
            {var subQ3=sQuery(id+"F7.wireOp",EDGE,"E70.left");Q0=makeQuery(id+"F7.imprint","IMPRINT",FACE,{"disambiguationData":[TD([[makeQuery(id+"F7.imprint","IMPRINT",EDGE,{"derivedFrom":subQ3}),-1.0]])]});}
            var Q1;
            {var subQ1=sQuery(id+"F7.wireOp",EDGE,"E66.top");Q1=makeQuery(id+"F7.imprint","IMPRINT",FACE,{"disambiguationData":[TD([[makeQuery(id+"F7.imprint","IMPRINT",EDGE,{"derivedFrom":subQ1}),1.0]])]});}
            var Q2;
            {var subQ6=sQuery(id+"F7.wireOp",EDGE,"E66.bottom");Q2=makeQuery(id+"F7.imprint","IMPRINT",FACE,{"disambiguationData":[TD([[makeQuery(id+"F7.imprint","IMPRINT",EDGE,{"derivedFrom":subQ6}),-1.0]])]});}
            var Q3;
            {var subQ3=sQuery(id+"F7.wireOp",EDGE,"E70.right");Q3=makeQuery(id+"F7.imprint","IMPRINT",FACE,{"disambiguationData":[TD([[makeQuery(id+"F7.imprint","IMPRINT",EDGE,{"derivedFrom":subQ3}),1.0]])]});}
            extrude(context, id + "F8", {"entities" : qUnion([Q0, Q1, Q2, Q3]), "depth" : 5 * mm});
        }
        {
            var Q0;
            {var subQ11=sQuery(id+"F7.wireOp",EDGE,"E72.bottom");Q0=makeQuery(id+"F7.imprint","IMPRINT",FACE,{"disambiguationData":[TD([[makeQuery(id+"F7.imprint","IMPRINT",EDGE,{"derivedFrom":subQ11}),-1.0]])]});}
            var Q1;
            {var subQ5=sQuery(id+"F7.wireOp",EDGE,"E73.right");Q1=makeQuery(id+"F7.imprint","IMPRINT",FACE,{"disambiguationData":[TD([[makeQuery(id+"F7.imprint","IMPRINT",EDGE,{"derivedFrom":subQ5}),-1.0]])]});}
            var Q2;
            {var subQ5=sQuery(id+"F7.wireOp",EDGE,"E74.left");Q2=makeQuery(id+"F7.imprint","IMPRINT",FACE,{"disambiguationData":[TD([[makeQuery(id+"F7.imprint","IMPRINT",EDGE,{"derivedFrom":subQ5}),1.0]])]});}
            var Q3;
            {var subQ0=sQuery(id+"F7.wireOp",EDGE,"E74.bottom");Q3=makeQuery(id+"F7.imprint","IMPRINT",FACE,{"disambiguationData":[TD([[makeQuery(id+"F7.imprint","IMPRINT",EDGE,{"derivedFrom":subQ0}),-1.0]])]});}
            var Q4;
            {var subQ2=sQuery(id+"F7.wireOp",EDGE,"E72.top");Q4=makeQuery(id+"F7.imprint","IMPRINT",FACE,{"disambiguationData":[TD([[makeQuery(id+"F7.imprint","IMPRINT",EDGE,{"derivedFrom":subQ2}),1.0]])]});}
            var Q5;
            {var subQ0=sQuery(id+"F7.wireOp",EDGE,"E73.bottom");Q5=makeQuery(id+"F7.imprint","IMPRINT",FACE,{"disambiguationData":[TD([[makeQuery(id+"F7.imprint","IMPRINT",EDGE,{"derivedFrom":subQ0}),-1.0]])]});}
            extrude(context, id + "F9", {"entities" : qUnion([Q0, Q1, Q2, Q3, Q4, Q5]), "depth" : 1 * mm});
        }
        {
            var Q0;
            {var subQ5=sQuery(id+"F7.wireOp",EDGE,"E74.right");Q0=makeQuery(id+"F7.imprint","IMPRINT",FACE,{"disambiguationData":[TD([[makeQuery(id+"F7.imprint","IMPRINT",EDGE,{"derivedFrom":subQ5}),-1.0]])]});}
            var Q1;
            {var subQ5=sQuery(id+"F7.wireOp",EDGE,"E74.left");Q1=makeQuery(id+"F7.imprint","IMPRINT",FACE,{"disambiguationData":[TD([[makeQuery(id+"F7.imprint","IMPRINT",EDGE,{"derivedFrom":subQ5}),1.0]])]});}
            var Q2;
            {var subQ5=sQuery(id+"F7.wireOp",EDGE,"E73.right");Q2=makeQuery(id+"F7.imprint","IMPRINT",FACE,{"disambiguationData":[TD([[makeQuery(id+"F7.imprint","IMPRINT",EDGE,{"derivedFrom":subQ5}),-1.0]])]});}
            var Q3;
            {var subQ5=sQuery(id+"F7.wireOp",EDGE,"E73.left");Q3=makeQuery(id+"F7.imprint","IMPRINT",FACE,{"disambiguationData":[TD([[makeQuery(id+"F7.imprint","IMPRINT",EDGE,{"derivedFrom":subQ5}),1.0]])]});}
            extrude(context, id + "F10", {"entities" : qUnion([Q0, Q1, Q2, Q3]), "operationType" : NewBodyOperationType.ADD, "oppositeDirection" : true, "depth" : 5 * mm});
        }
        {
            var Q0;
            Q0=makeQuery(id+"F9.opExtrude","CAP_FACE",FACE,{"disambiguationData":[OSD([sQuery(id+"F7.wireOp",EDGE,"E72.bottom"),sQuery(id+"F7.wireOp",EDGE,"E72.top"),sQuery(id+"F7.wireOp",EDGE,"E72.left"),sQuery(id+"F7.wireOp",EDGE,"E72.right"),sQuery(id+"F7.wireOp",EDGE,"E73.left"),sQuery(id+"F7.wireOp",EDGE,"E74.right"),sQuery(id+"F7.wireOp",EDGE,"E75.bottom"),sQuery(id+"F7.wireOp",EDGE,"E75.top"),sQuery(id+"F7.wireOp",EDGE,"E75.left"),sQuery(id+"F7.wireOp",EDGE,"E75.right")])],"isStart":false});
            var sketch = newSketch(context, id + "F11", { "sketchPlane" : qUnion([Q0])});
            skPoint(sketch, "E76.0", {"position": v(-121.72, 49.3) * mm});
            skLineSegment(sketch, "E77.bottom", {"start": v(-112.62, 40.2) * mm, "end": v(-130.82, 40.2) * mm});
            skLineSegment(sketch, "E77.top", {"start": v(-112.62, 58.4) * mm, "end": v(-130.82, 58.4) * mm});
            skLineSegment(sketch, "E77.left", {"start": v(-112.62, 40.2) * mm, "end": v(-112.62, 58.4) * mm});
            skLineSegment(sketch, "E77.right", {"start": v(-130.82, 40.2) * mm, "end": v(-130.82, 58.4) * mm});
            skLineSegment(sketch, "E78.0", {"start": v(-131.82, 39.2) * mm, "end": v(-131.82, 59.4) * mm});
            skLineSegment(sketch, "E78.1", {"start": v(-111.62, 39.2) * mm, "end": v(-131.82, 39.2) * mm});
            skLineSegment(sketch, "E78.2", {"start": v(-111.62, 39.2) * mm, "end": v(-111.62, 59.4) * mm});
            skLineSegment(sketch, "E78.3", {"start": v(-111.62, 59.4) * mm, "end": v(-131.82, 59.4) * mm});
            skSolve(sketch);
        }
        {
            var Q0;
            Q0=makeQuery(id+"F11.imprint","IMPRINT",FACE,{"disambiguationData":[TD([[makeQuery(id+"F11.imprint","IMPRINT",EDGE,{"derivedFrom":sQuery(id+"F11.wireOp",EDGE,"E77.bottom")}),1.0]])]});
            extrude(context, id + "F12", {"entities" : qUnion([Q0]), "operationType" : NewBodyOperationType.ADD, "depth" : 5 * mm});
        }
    });
